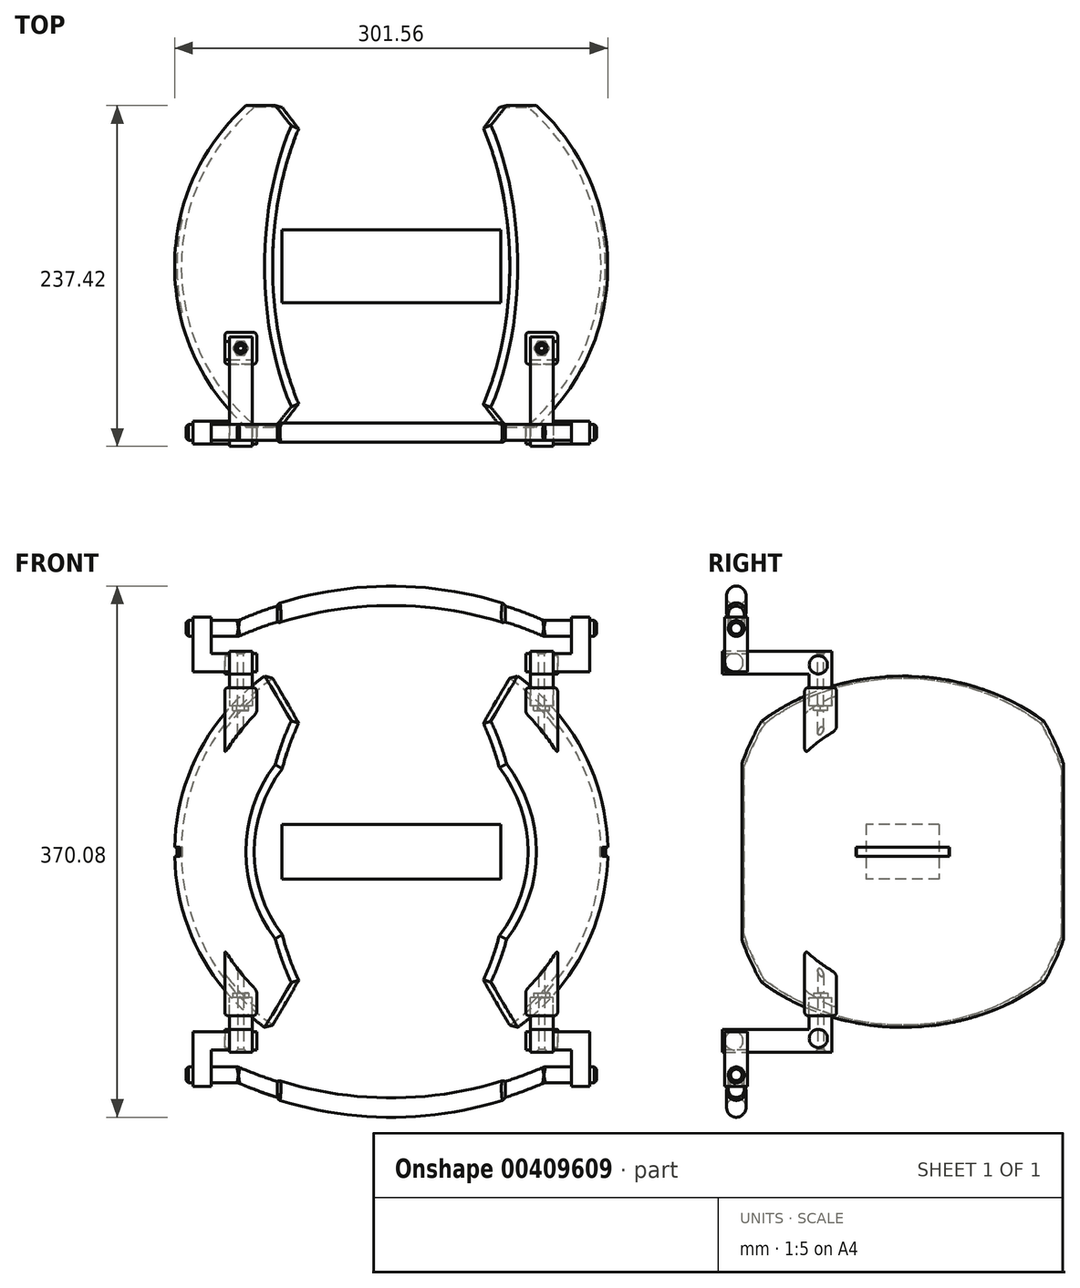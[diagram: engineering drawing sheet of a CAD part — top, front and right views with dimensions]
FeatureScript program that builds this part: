
annotation { "Feature Type Name" : "Feature", "Feature Type Description" : "" }
export const myFeature = defineFeature(function(context is Context, id is Id, definition is map)
    precondition{}
    {
        {
            var Q0;
            Q0=qCreatedBy(makeId("Right.planeOp"),FACE);
            var sketch = newSketch(context, id + "F0", { "sketchPlane" : qUnion([Q0])});
            skArc(sketch, "E0", {"start": v(0, -146.11) * mm, "mid": v(146.11, 0) * mm, "end": v(0, 146.11) * mm});
            skArc(sketch, "E1", {"start": v(0, -150.81) * mm, "mid": v(150.81, 0) * mm, "end": v(0, 150.81) * mm});
            skLineSegment(sketch, "E2", {"start": v(0, 150.81) * mm, "end": v(0, 146.11) * mm});
            skLineSegment(sketch, "E3.trimOffspring", {"start": v(0, 0) * mm, "end": v(0, -150.81) * mm});
            skSolve(sketch);
        }
        {
            var Q0;
            Q0 = qSketchRegion(id + "F0", true);
            var Q1;
            Q1=sQuery(id+"F0.wireOp",EDGE,"E3.trimOffspring");
            revolve(context, id + "F1", {"entities" : qUnion([Q0]), "axis" : qUnion([Q1]), "revolveType" : RevolveType.FULL});
        }
        {
            var Q0;
            Q0=qCreatedBy(makeId("Top.planeOp"),FACE);
            var sketch = newSketch(context, id + "F2", { "sketchPlane" : qUnion([Q0])});
            skEllipse(sketch, "E4", {"center": v(0, 0) * mm, "majorRadius": 152.4 * mm, "minorRadius": 82.55 * mm, "majorAxis": v(0, -1)});
            skSolve(sketch);
        }
        {
            var Q0;
            Q0 = qSketchRegion(id + "F2", true);
            extrude(context, id + "F3", {"entities" : qUnion([Q0]), "operationType" : NewBodyOperationType.REMOVE, "endBound" : BoundingType.SYMMETRIC, "oppositeDirection" : true, "depth" : 304.8 * mm});
        }
        {
            var Q0;
            Q0=qCreatedBy(makeId("Front.planeOp"),FACE);
            var sketch = newSketch(context, id + "F4", { "sketchPlane" : qUnion([Q0])});
            skArc(sketch, "E5", {"start": v(-74.85, 58.9) * mm, "mid": v(-95.25, 0) * mm, "end": v(-74.85, -58.9) * mm});
            skEllipticalArc(sketch, "E6", {});
            skEllipticalArc(sketch, "E7.trimOffspring", {});
            skArc(sketch, "E8.trimOffspring", {"start": v(74.85, -58.9) * mm, "mid": v(95.25, 0) * mm, "end": v(74.85, 58.9) * mm});
            const initialGuessF4  = {"E6": [0, 0, 0, -1, 0.1397, 0.08255, 5.147638887361655, 1.1355464198179313], "E7.trimOffspring": [0, 0, 0, -1, 0.1397, 0.08255, 2.006046233771862, 4.277139073407724]};
            skSetInitialGuess(sketch, initialGuessF4);
            skSolve(sketch);
        }
        {
            var Q0;
            Q0 = qSketchRegion(id + "F4", true);
            extrude(context, id + "F5", {"entities" : qUnion([Q0]), "operationType" : NewBodyOperationType.REMOVE, "endBound" : BoundingType.SYMMETRIC, "oppositeDirection" : true, "depth" : 304.8 * mm});
        }
        {
            var Q0;
            {var subQ0=makeQuery(id+"F1.opRevolve","SWEPT_FACE",FACE,{"disambiguationData":[OSD([sQuery(id+"F0.wireOp",EDGE,"E1")])]});var subQ1=makeQuery(id+"F3.opExtrude","SWEPT_FACE",FACE,{"disambiguationData":[OSD([sQuery(id+"F2.wireOp",EDGE,"E4")])]});Q0=makeQuery(id+"F5.boolean.opBoolean","SPLIT",EDGE,{"disambiguationData":[TD([makeQuery(id+"F5.opExtrude","SWEPT_FACE",FACE,{"disambiguationData":[OSD([sQuery(id+"F4.wireOp",EDGE,"E7.trimOffspring")])]})])],"derivedFrom":makeQuery(id+"F3.boolean.opBoolean","INTERSECT",EDGE,{"disambiguationData":[OD(1.0)],"derivedFrom":[subQ0,subQ1]})});}
            var Q1;
            Q1=makeQuery(id+"F5.boolean.opBoolean","INTERSECT",EDGE,{"disambiguationData":[OD(0.0)],"derivedFrom":[makeQuery(id+"F3.boolean.opBoolean","SPLIT",FACE,{"disambiguationData":[OD(1.0)],"derivedFrom":makeQuery(id+"F1.opRevolve","SWEPT_FACE",FACE,{"disambiguationData":[OSD([sQuery(id+"F0.wireOp",EDGE,"E1")])]})}),makeQuery(id+"F5.opExtrude","SWEPT_FACE",FACE,{"disambiguationData":[OSD([sQuery(id+"F4.wireOp",EDGE,"E5")])]})]});
            var Q2;
            Q2=makeQuery(id+"F5.boolean.opBoolean","INTERSECT",EDGE,{"disambiguationData":[OD(1.0)],"derivedFrom":[makeQuery(id+"F3.boolean.opBoolean","SPLIT",FACE,{"disambiguationData":[OD(1.0)],"derivedFrom":makeQuery(id+"F1.opRevolve","SWEPT_FACE",FACE,{"disambiguationData":[OSD([sQuery(id+"F0.wireOp",EDGE,"E1")])]})}),makeQuery(id+"F5.opExtrude","SWEPT_FACE",FACE,{"disambiguationData":[OSD([sQuery(id+"F4.wireOp",EDGE,"E5")])]})]});
            var Q3;
            {var subQ0=makeQuery(id+"F1.opRevolve","SWEPT_FACE",FACE,{"disambiguationData":[OSD([sQuery(id+"F0.wireOp",EDGE,"E1")])]});var subQ1=makeQuery(id+"F3.opExtrude","SWEPT_FACE",FACE,{"disambiguationData":[OSD([sQuery(id+"F2.wireOp",EDGE,"E4")])]});Q3=makeQuery(id+"F5.boolean.opBoolean","SPLIT",EDGE,{"disambiguationData":[TD([makeQuery(id+"F5.opExtrude","SWEPT_FACE",FACE,{"disambiguationData":[OSD([sQuery(id+"F4.wireOp",EDGE,"E6")])]})])],"derivedFrom":makeQuery(id+"F3.boolean.opBoolean","INTERSECT",EDGE,{"disambiguationData":[OD(1.0)],"derivedFrom":[subQ0,subQ1]})});}
            var Q4;
            {var subQ0=makeQuery(id+"F1.opRevolve","SWEPT_FACE",FACE,{"disambiguationData":[OSD([sQuery(id+"F0.wireOp",EDGE,"E1")])]});var subQ1=makeQuery(id+"F3.opExtrude","SWEPT_FACE",FACE,{"disambiguationData":[OSD([sQuery(id+"F2.wireOp",EDGE,"E4")])]});Q4=makeQuery(id+"F5.boolean.opBoolean","SPLIT",EDGE,{"disambiguationData":[TD([makeQuery(id+"F5.opExtrude","SWEPT_FACE",FACE,{"disambiguationData":[OSD([sQuery(id+"F4.wireOp",EDGE,"E7.trimOffspring")])]})])],"derivedFrom":makeQuery(id+"F3.boolean.opBoolean","INTERSECT",EDGE,{"disambiguationData":[OD(0.0)],"derivedFrom":[subQ0,subQ1]})});}
            var Q5;
            Q5=makeQuery(id+"F5.boolean.opBoolean","INTERSECT",EDGE,{"disambiguationData":[OD(1.0)],"derivedFrom":[makeQuery(id+"F3.boolean.opBoolean","SPLIT",FACE,{"disambiguationData":[OD(0.0)],"derivedFrom":makeQuery(id+"F1.opRevolve","SWEPT_FACE",FACE,{"disambiguationData":[OSD([sQuery(id+"F0.wireOp",EDGE,"E1")])]})}),makeQuery(id+"F5.opExtrude","SWEPT_FACE",FACE,{"disambiguationData":[OSD([sQuery(id+"F4.wireOp",EDGE,"E8.trimOffspring")])]})]});
            var Q6;
            Q6=makeQuery(id+"F5.boolean.opBoolean","INTERSECT",EDGE,{"disambiguationData":[OD(0.0)],"derivedFrom":[makeQuery(id+"F3.boolean.opBoolean","SPLIT",FACE,{"disambiguationData":[OD(0.0)],"derivedFrom":makeQuery(id+"F1.opRevolve","SWEPT_FACE",FACE,{"disambiguationData":[OSD([sQuery(id+"F0.wireOp",EDGE,"E1")])]})}),makeQuery(id+"F5.opExtrude","SWEPT_FACE",FACE,{"disambiguationData":[OSD([sQuery(id+"F4.wireOp",EDGE,"E8.trimOffspring")])]})]});
            var Q7;
            {var subQ0=makeQuery(id+"F1.opRevolve","SWEPT_FACE",FACE,{"disambiguationData":[OSD([sQuery(id+"F0.wireOp",EDGE,"E1")])]});var subQ1=makeQuery(id+"F3.opExtrude","SWEPT_FACE",FACE,{"disambiguationData":[OSD([sQuery(id+"F2.wireOp",EDGE,"E4")])]});Q7=makeQuery(id+"F5.boolean.opBoolean","SPLIT",EDGE,{"disambiguationData":[TD([makeQuery(id+"F5.opExtrude","SWEPT_FACE",FACE,{"disambiguationData":[OSD([sQuery(id+"F4.wireOp",EDGE,"E6")])]})])],"derivedFrom":makeQuery(id+"F3.boolean.opBoolean","INTERSECT",EDGE,{"disambiguationData":[OD(0.0)],"derivedFrom":[subQ0,subQ1]})});}
            chamfer(context, id + "F6", {"entities" : qUnion([Q0, Q1, Q2, Q3, Q4, Q5, Q6, Q7]), "chamferType" : ChamferType.OFFSET_ANGLE, "width" : 7.62 * mm, "oppositeDirection" : false, "angle" : 55 * degree, "tangentPropagation" : true});
        }
        {
            var Q0;
            Q0=makeQuery(id+"F5.boolean.opBoolean","INTERSECT",EDGE,{"disambiguationData":[OD(0.0)],"derivedFrom":[makeQuery(id+"F3.boolean.opBoolean","SPLIT",FACE,{"disambiguationData":[OD(1.0)],"derivedFrom":makeQuery(id+"F1.opRevolve","SWEPT_FACE",FACE,{"disambiguationData":[OSD([sQuery(id+"F0.wireOp",EDGE,"E1")])]})}),makeQuery(id+"F5.opExtrude","SWEPT_FACE",FACE,{"disambiguationData":[OSD([sQuery(id+"F4.wireOp",EDGE,"E7.trimOffspring")])]})]});
            var Q1;
            Q1=makeQuery(id+"F5.boolean.opBoolean","INTERSECT",EDGE,{"disambiguationData":[OD(1.0)],"derivedFrom":[makeQuery(id+"F3.boolean.opBoolean","SPLIT",FACE,{"disambiguationData":[OD(1.0)],"derivedFrom":makeQuery(id+"F1.opRevolve","SWEPT_FACE",FACE,{"disambiguationData":[OSD([sQuery(id+"F0.wireOp",EDGE,"E1")])]})}),makeQuery(id+"F5.opExtrude","SWEPT_FACE",FACE,{"disambiguationData":[OSD([sQuery(id+"F4.wireOp",EDGE,"E7.trimOffspring")])]})]});
            var Q2;
            Q2=makeQuery(id+"F5.boolean.opBoolean","INTERSECT",EDGE,{"disambiguationData":[OD(1.0)],"derivedFrom":[makeQuery(id+"F3.boolean.opBoolean","SPLIT",FACE,{"disambiguationData":[OD(1.0)],"derivedFrom":makeQuery(id+"F1.opRevolve","SWEPT_FACE",FACE,{"disambiguationData":[OSD([sQuery(id+"F0.wireOp",EDGE,"E1")])]})}),makeQuery(id+"F5.opExtrude","SWEPT_FACE",FACE,{"disambiguationData":[OSD([sQuery(id+"F4.wireOp",EDGE,"E6")])]})]});
            var Q3;
            Q3=makeQuery(id+"F5.boolean.opBoolean","INTERSECT",EDGE,{"disambiguationData":[OD(0.0)],"derivedFrom":[makeQuery(id+"F3.boolean.opBoolean","SPLIT",FACE,{"disambiguationData":[OD(1.0)],"derivedFrom":makeQuery(id+"F1.opRevolve","SWEPT_FACE",FACE,{"disambiguationData":[OSD([sQuery(id+"F0.wireOp",EDGE,"E1")])]})}),makeQuery(id+"F5.opExtrude","SWEPT_FACE",FACE,{"disambiguationData":[OSD([sQuery(id+"F4.wireOp",EDGE,"E6")])]})]});
            var Q4;
            Q4=makeQuery(id+"F5.boolean.opBoolean","INTERSECT",EDGE,{"disambiguationData":[OD(0.0)],"derivedFrom":[makeQuery(id+"F3.boolean.opBoolean","SPLIT",FACE,{"disambiguationData":[OD(0.0)],"derivedFrom":makeQuery(id+"F1.opRevolve","SWEPT_FACE",FACE,{"disambiguationData":[OSD([sQuery(id+"F0.wireOp",EDGE,"E1")])]})}),makeQuery(id+"F5.opExtrude","SWEPT_FACE",FACE,{"disambiguationData":[OSD([sQuery(id+"F4.wireOp",EDGE,"E7.trimOffspring")])]})]});
            var Q5;
            Q5=makeQuery(id+"F5.boolean.opBoolean","INTERSECT",EDGE,{"disambiguationData":[OD(1.0)],"derivedFrom":[makeQuery(id+"F3.boolean.opBoolean","SPLIT",FACE,{"disambiguationData":[OD(0.0)],"derivedFrom":makeQuery(id+"F1.opRevolve","SWEPT_FACE",FACE,{"disambiguationData":[OSD([sQuery(id+"F0.wireOp",EDGE,"E1")])]})}),makeQuery(id+"F5.opExtrude","SWEPT_FACE",FACE,{"disambiguationData":[OSD([sQuery(id+"F4.wireOp",EDGE,"E7.trimOffspring")])]})]});
            var Q6;
            Q6=makeQuery(id+"F5.boolean.opBoolean","INTERSECT",EDGE,{"disambiguationData":[OD(0.0)],"derivedFrom":[makeQuery(id+"F3.boolean.opBoolean","SPLIT",FACE,{"disambiguationData":[OD(0.0)],"derivedFrom":makeQuery(id+"F1.opRevolve","SWEPT_FACE",FACE,{"disambiguationData":[OSD([sQuery(id+"F0.wireOp",EDGE,"E1")])]})}),makeQuery(id+"F5.opExtrude","SWEPT_FACE",FACE,{"disambiguationData":[OSD([sQuery(id+"F4.wireOp",EDGE,"E6")])]})]});
            var Q7;
            Q7=makeQuery(id+"F5.boolean.opBoolean","INTERSECT",EDGE,{"disambiguationData":[OD(1.0)],"derivedFrom":[makeQuery(id+"F3.boolean.opBoolean","SPLIT",FACE,{"disambiguationData":[OD(0.0)],"derivedFrom":makeQuery(id+"F1.opRevolve","SWEPT_FACE",FACE,{"disambiguationData":[OSD([sQuery(id+"F0.wireOp",EDGE,"E1")])]})}),makeQuery(id+"F5.opExtrude","SWEPT_FACE",FACE,{"disambiguationData":[OSD([sQuery(id+"F4.wireOp",EDGE,"E6")])]})]});
            chamfer(context, id + "F7", {"entities" : qUnion([Q0, Q1, Q2, Q3, Q4, Q5, Q6, Q7]), "chamferType" : ChamferType.OFFSET_ANGLE, "width" : 7.62 * mm, "oppositeDirection" : false, "angle" : 55 * degree, "tangentPropagation" : true});
        }
        {
            var Q0;
            Q0=qCreatedBy(makeId("Front.planeOp"),FACE);
            var sketch = newSketch(context, id + "F8", { "sketchPlane" : qUnion([Q0])});
            skLineSegment(sketch, "E9", {"start": v(-149.23, 0) * mm, "end": v(149.23, 0) * mm});
            skLineSegment(sketch, "E10", {"start": v(-149.2, 3.1) * mm, "end": v(-152.4, 3.18) * mm});
            skLineSegment(sketch, "E11", {"start": v(-149.2, -3.1) * mm, "end": v(-152.4, -3.18) * mm});
            skLineSegment(sketch, "E12", {"start": v(149.2, 3.1) * mm, "end": v(152.4, 3.17) * mm});
            skLineSegment(sketch, "E13", {"start": v(149.2, -3.1) * mm, "end": v(152.4, -3.18) * mm});
            skLineSegment(sketch, "E14", {"start": v(-152.4, 3.18) * mm, "end": v(-152.4, -3.18) * mm});
            skLineSegment(sketch, "E15", {"start": v(152.4, 0) * mm, "end": v(152.4, 3.18) * mm});
            skLineSegment(sketch, "E16", {"start": v(152.4, 0) * mm, "end": v(152.4, -3.17) * mm});
            skPoint(sketch, "E17.orphan", {"position": v(-174.04, 0) * mm});
            skArc(sketch, "E18", {"start": v(-149.2, 3.1) * mm, "mid": v(-149.23, 0) * mm, "end": v(-149.2, -3.1) * mm});
            skArc(sketch, "E19.trimOffspring", {"start": v(149.2, -3.1) * mm, "mid": v(149.23, 0) * mm, "end": v(149.2, 3.1) * mm});
            skLineSegment(sketch, "E20", {"start": v(0, -61.34) * mm, "end": v(0, 25.34) * mm});
            skSolve(sketch);
        }
        {
            var Q0;
            Q0 = qSketchRegion(id + "F8", true);
            var Q1;
            Q1=sQuery(id+"F8.wireOp",EDGE,"E20");
            revolve(context, id + "F9", {"operationType" : NewBodyOperationType.REMOVE, "entities" : qUnion([Q0]), "axis" : qUnion([Q1]), "revolveType" : RevolveType.SYMMETRIC, "angle" : 25 * degree});
        }
        {
            var Q0;
            Q0=qCreatedBy(makeId("Top.planeOp"),FACE);
            cPlane(context, id + "F10", {"entities" : qUnion([Q0]), "cplaneType" : CPlaneType.OFFSET, "offset" : 127 * mm, "width" : 152.4 * mm, "height" : 152.4 * mm});
        }
        {
            var Q0;
            Q0=qCreatedBy(makeId("Top.planeOp"),FACE);
            cPlane(context, id + "F11", {"entities" : qUnion([Q0]), "cplaneType" : CPlaneType.OFFSET, "offset" : 127 * mm, "oppositeDirection" : true, "width" : 152.4 * mm, "height" : 152.4 * mm});
        }
        {
            var Q0;
            Q0=qCreatedBy(id+"F10.planeOp",FACE);
            var sketch = newSketch(context, id + "F12", { "sketchPlane" : qUnion([Q0])});
            skPoint(sketch, "E21", {"position": v(-104.78, -57.15) * mm});
            skPoint(sketch, "E22", {"position": v(104.77, -57.15) * mm});
            skLineSegment(sketch, "E23.bottom", {"start": v(-93.66, -46.04) * mm, "end": v(-115.89, -46.04) * mm});
            skLineSegment(sketch, "E23.top", {"start": v(-93.66, -68.26) * mm, "end": v(-115.89, -68.26) * mm});
            skLineSegment(sketch, "E23.left", {"start": v(-93.66, -46.04) * mm, "end": v(-93.66, -68.26) * mm});
            skLineSegment(sketch, "E23.right", {"start": v(-115.89, -46.04) * mm, "end": v(-115.89, -68.26) * mm});
            skLineSegment(sketch, "E24.bottom", {"start": v(93.66, -46.04) * mm, "end": v(115.89, -46.04) * mm});
            skLineSegment(sketch, "E24.top", {"start": v(93.66, -68.26) * mm, "end": v(115.89, -68.26) * mm});
            skLineSegment(sketch, "E24.left", {"start": v(93.66, -46.04) * mm, "end": v(93.66, -68.26) * mm});
            skLineSegment(sketch, "E24.right", {"start": v(115.89, -46.04) * mm, "end": v(115.89, -68.26) * mm});
            skSolve(sketch);
        }
        {
            var Q0;
            Q0 = qSketchRegion(id + "F12", true);
            var Q1;
            Q1=makeQuery(id+"F3.boolean.opBoolean","SPLIT",FACE,{"disambiguationData":[OD(1.0)],"derivedFrom":makeQuery(id+"F1.opRevolve","SWEPT_FACE",FACE,{"disambiguationData":[OSD([sQuery(id+"F0.wireOp",EDGE,"E1")])]})});
            var Q2;
            Q2=makeQuery(id+"F3.boolean.opBoolean","SPLIT",FACE,{"disambiguationData":[OD(1.0)],"derivedFrom":makeQuery(id+"F1.opRevolve","SWEPT_FACE",FACE,{"disambiguationData":[OSD([sQuery(id+"F0.wireOp",EDGE,"E1")])]})});
            extrude(context, id + "F13", {"entities" : qUnion([Q0]), "operationType" : NewBodyOperationType.ADD, "endBound" : BoundingType.UP_TO_SURFACE, "oppositeDirection" : true, "endBoundEntityFace" : qUnion([Q1]), "depth" : 17.78 * mm, "hasSecondDirection" : true, "secondDirectionOppositeDirection" : true, "secondDirectionBoundEntityFace" : qUnion([Q2]), "secondDirectionDepth" : 12.7 * mm});
        }
        {
            var Q0;
            Q0=qCreatedBy(id+"F11.planeOp",FACE);
            var sketch = newSketch(context, id + "F14", { "sketchPlane" : qUnion([Q0])});
            skPoint(sketch, "E25", {"position": v(-104.77, -57.15) * mm});
            skPoint(sketch, "E26", {"position": v(104.78, -57.15) * mm});
            skLineSegment(sketch, "E27.bottom", {"start": v(-93.66, -46.04) * mm, "end": v(-115.89, -46.04) * mm});
            skLineSegment(sketch, "E27.top", {"start": v(-93.66, -68.26) * mm, "end": v(-115.89, -68.26) * mm});
            skLineSegment(sketch, "E27.left", {"start": v(-93.66, -46.04) * mm, "end": v(-93.66, -68.26) * mm});
            skLineSegment(sketch, "E27.right", {"start": v(-115.89, -46.04) * mm, "end": v(-115.89, -68.26) * mm});
            skLineSegment(sketch, "E28.bottom", {"start": v(93.66, -46.04) * mm, "end": v(115.89, -46.04) * mm});
            skLineSegment(sketch, "E28.top", {"start": v(93.66, -68.26) * mm, "end": v(115.89, -68.26) * mm});
            skLineSegment(sketch, "E28.left", {"start": v(93.66, -46.04) * mm, "end": v(93.66, -68.26) * mm});
            skLineSegment(sketch, "E28.right", {"start": v(115.89, -46.04) * mm, "end": v(115.89, -68.26) * mm});
            skSolve(sketch);
        }
        {
            var Q0;
            Q0 = qSketchRegion(id + "F14", true);
            var Q1;
            Q1=makeQuery(id+"F3.boolean.opBoolean","SPLIT",FACE,{"disambiguationData":[OD(1.0)],"derivedFrom":makeQuery(id+"F1.opRevolve","SWEPT_FACE",FACE,{"disambiguationData":[OSD([sQuery(id+"F0.wireOp",EDGE,"E1")])]})});
            extrude(context, id + "F15", {"entities" : qUnion([Q0]), "operationType" : NewBodyOperationType.ADD, "endBound" : BoundingType.UP_TO_SURFACE, "endBoundEntityFace" : qUnion([Q1]), "depth" : 25.4 * mm, "hasSecondDirection" : true, "secondDirectionOppositeDirection" : false, "secondDirectionDepth" : 12.7 * mm});
        }
        {
            var Q0;
            Q0=makeQuery(id+"F13.opExtrude","SWEPT_EDGE",EDGE,{"disambiguationData":[OSD([sQuery(id+"F12.wireOp",EDGE,"E23.top"),sQuery(id+"F12.wireOp",EDGE,"E23.right")])]});
            var Q1;
            Q1=makeQuery(id+"F13.opExtrude","SWEPT_EDGE",EDGE,{"disambiguationData":[OSD([sQuery(id+"F12.wireOp",EDGE,"E23.top"),sQuery(id+"F12.wireOp",EDGE,"E23.left")])]});
            var Q2;
            Q2=makeQuery(id+"F13.opExtrude","SWEPT_EDGE",EDGE,{"disambiguationData":[OSD([sQuery(id+"F12.wireOp",EDGE,"E23.bottom"),sQuery(id+"F12.wireOp",EDGE,"E23.left")])]});
            var Q3;
            Q3=makeQuery(id+"F13.opExtrude","SWEPT_EDGE",EDGE,{"disambiguationData":[OSD([sQuery(id+"F12.wireOp",EDGE,"E23.bottom"),sQuery(id+"F12.wireOp",EDGE,"E23.right")])]});
            var Q4;
            Q4=makeQuery(id+"F13.opExtrude","CAP_EDGE",EDGE,{"disambiguationData":[OSD([sQuery(id+"F12.wireOp",EDGE,"E23.right")])],"isStart":true});
            var Q5;
            Q5=makeQuery(id+"F13.opExtrude","CAP_EDGE",EDGE,{"disambiguationData":[OSD([sQuery(id+"F12.wireOp",EDGE,"E23.bottom")])],"isStart":true});
            var Q6;
            Q6=makeQuery(id+"F13.opExtrude","CAP_EDGE",EDGE,{"disambiguationData":[OSD([sQuery(id+"F12.wireOp",EDGE,"E23.left")])],"isStart":true});
            var Q7;
            Q7=makeQuery(id+"F13.opExtrude","CAP_EDGE",EDGE,{"disambiguationData":[OSD([sQuery(id+"F12.wireOp",EDGE,"E23.top")])],"isStart":true});
            var Q8;
            Q8=makeQuery(id+"F13.opExtrude","SWEPT_EDGE",EDGE,{"disambiguationData":[OSD([sQuery(id+"F12.wireOp",EDGE,"E24.bottom"),sQuery(id+"F12.wireOp",EDGE,"E24.left")])]});
            var Q9;
            Q9=makeQuery(id+"F13.opExtrude","SWEPT_EDGE",EDGE,{"disambiguationData":[OSD([sQuery(id+"F12.wireOp",EDGE,"E24.top"),sQuery(id+"F12.wireOp",EDGE,"E24.left")])]});
            var Q10;
            Q10=makeQuery(id+"F13.opExtrude","SWEPT_EDGE",EDGE,{"disambiguationData":[OSD([sQuery(id+"F12.wireOp",EDGE,"E24.top"),sQuery(id+"F12.wireOp",EDGE,"E24.right")])]});
            var Q11;
            Q11=makeQuery(id+"F13.opExtrude","SWEPT_EDGE",EDGE,{"disambiguationData":[OSD([sQuery(id+"F12.wireOp",EDGE,"E24.bottom"),sQuery(id+"F12.wireOp",EDGE,"E24.right")])]});
            var Q12;
            Q12=makeQuery(id+"F13.opExtrude","CAP_EDGE",EDGE,{"disambiguationData":[OSD([sQuery(id+"F12.wireOp",EDGE,"E24.bottom")])],"isStart":true});
            var Q13;
            Q13=makeQuery(id+"F13.opExtrude","CAP_EDGE",EDGE,{"disambiguationData":[OSD([sQuery(id+"F12.wireOp",EDGE,"E24.left")])],"isStart":true});
            var Q14;
            Q14=makeQuery(id+"F13.opExtrude","CAP_EDGE",EDGE,{"disambiguationData":[OSD([sQuery(id+"F12.wireOp",EDGE,"E24.top")])],"isStart":true});
            var Q15;
            Q15=makeQuery(id+"F13.opExtrude","CAP_EDGE",EDGE,{"disambiguationData":[OSD([sQuery(id+"F12.wireOp",EDGE,"E24.right")])],"isStart":true});
            var Q16;
            Q16=makeQuery(id+"F15.opExtrude","SWEPT_EDGE",EDGE,{"disambiguationData":[OSD([sQuery(id+"F14.wireOp",EDGE,"E27.bottom"),sQuery(id+"F14.wireOp",EDGE,"E27.right")])]});
            var Q17;
            Q17=makeQuery(id+"F15.opExtrude","SWEPT_EDGE",EDGE,{"disambiguationData":[OSD([sQuery(id+"F14.wireOp",EDGE,"E27.top"),sQuery(id+"F14.wireOp",EDGE,"E27.right")])]});
            var Q18;
            Q18=makeQuery(id+"F15.opExtrude","SWEPT_EDGE",EDGE,{"disambiguationData":[OSD([sQuery(id+"F14.wireOp",EDGE,"E27.top"),sQuery(id+"F14.wireOp",EDGE,"E27.left")])]});
            var Q19;
            Q19=makeQuery(id+"F15.opExtrude","SWEPT_EDGE",EDGE,{"disambiguationData":[OSD([sQuery(id+"F14.wireOp",EDGE,"E27.bottom"),sQuery(id+"F14.wireOp",EDGE,"E27.left")])]});
            var Q20;
            Q20=makeQuery(id+"F15.opExtrude","CAP_EDGE",EDGE,{"disambiguationData":[OSD([sQuery(id+"F14.wireOp",EDGE,"E27.right")])],"isStart":true});
            var Q21;
            Q21=makeQuery(id+"F15.opExtrude","CAP_EDGE",EDGE,{"disambiguationData":[OSD([sQuery(id+"F14.wireOp",EDGE,"E27.bottom")])],"isStart":true});
            var Q22;
            Q22=makeQuery(id+"F15.opExtrude","CAP_EDGE",EDGE,{"disambiguationData":[OSD([sQuery(id+"F14.wireOp",EDGE,"E27.top")])],"isStart":true});
            var Q23;
            Q23=makeQuery(id+"F15.opExtrude","CAP_EDGE",EDGE,{"disambiguationData":[OSD([sQuery(id+"F14.wireOp",EDGE,"E27.left")])],"isStart":true});
            var Q24;
            Q24=makeQuery(id+"F15.opExtrude","SWEPT_EDGE",EDGE,{"disambiguationData":[OSD([sQuery(id+"F14.wireOp",EDGE,"E28.top"),sQuery(id+"F14.wireOp",EDGE,"E28.left")])]});
            var Q25;
            Q25=makeQuery(id+"F15.opExtrude","SWEPT_EDGE",EDGE,{"disambiguationData":[OSD([sQuery(id+"F14.wireOp",EDGE,"E28.top"),sQuery(id+"F14.wireOp",EDGE,"E28.right")])]});
            var Q26;
            Q26=makeQuery(id+"F15.opExtrude","SWEPT_EDGE",EDGE,{"disambiguationData":[OSD([sQuery(id+"F14.wireOp",EDGE,"E28.bottom"),sQuery(id+"F14.wireOp",EDGE,"E28.right")])]});
            var Q27;
            Q27=makeQuery(id+"F15.opExtrude","SWEPT_EDGE",EDGE,{"disambiguationData":[OSD([sQuery(id+"F14.wireOp",EDGE,"E28.bottom"),sQuery(id+"F14.wireOp",EDGE,"E28.left")])]});
            var Q28;
            Q28=makeQuery(id+"F15.opExtrude","CAP_EDGE",EDGE,{"disambiguationData":[OSD([sQuery(id+"F14.wireOp",EDGE,"E28.left")])],"isStart":true});
            var Q29;
            Q29=makeQuery(id+"F15.opExtrude","CAP_EDGE",EDGE,{"disambiguationData":[OSD([sQuery(id+"F14.wireOp",EDGE,"E28.top")])],"isStart":true});
            var Q30;
            Q30=makeQuery(id+"F15.opExtrude","CAP_EDGE",EDGE,{"disambiguationData":[OSD([sQuery(id+"F14.wireOp",EDGE,"E28.right")])],"isStart":true});
            var Q31;
            Q31=makeQuery(id+"F15.opExtrude","CAP_EDGE",EDGE,{"disambiguationData":[OSD([sQuery(id+"F14.wireOp",EDGE,"E28.bottom")])],"isStart":true});
            fillet(context, id + "F16", {"entities" : qUnion([Q0, Q1, Q2, Q3, Q4, Q5, Q6, Q7, Q8, Q9, Q10, Q11, Q12, Q13, Q14, Q15, Q16, Q17, Q18, Q19, Q20, Q21, Q22, Q23, Q24, Q25, Q26, Q27, Q28, Q29, Q30, Q31]), "radius" : 2.38 * mm, "tangentPropagation" : true, "allowEdgeOverflow" : false});
        }
        {
            var Q0;
            Q0=makeQuery(id+"F13.opExtrude","CAP_FACE",FACE,{"disambiguationData":[OSD([sQuery(id+"F12.wireOp",EDGE,"E24.bottom"),sQuery(id+"F12.wireOp",EDGE,"E24.top"),sQuery(id+"F12.wireOp",EDGE,"E24.left"),sQuery(id+"F12.wireOp",EDGE,"E24.right")])],"isStart":true});
            var sketch = newSketch(context, id + "F17", { "sketchPlane" : qUnion([Q0])});
            skLineSegment(sketch, "E29", {"start": v(96.05, -57.15) * mm, "end": v(113.5, -57.15) * mm});
            skLineSegment(sketch, "E30.bottom", {"start": v(112.71, -49.21) * mm, "end": v(96.84, -49.21) * mm});
            skLineSegment(sketch, "E30.top", {"start": v(112.71, -65.09) * mm, "end": v(96.84, -65.09) * mm});
            skLineSegment(sketch, "E30.left", {"start": v(112.71, -49.21) * mm, "end": v(112.71, -65.09) * mm});
            skLineSegment(sketch, "E30.right", {"start": v(96.84, -49.21) * mm, "end": v(96.84, -65.09) * mm});
            skPoint(sketch, "E30.middle", {"position": v(104.77, -57.15) * mm});
            skSolve(sketch);
        }
        {
            var Q0;
            Q0=makeQuery(id+"F13.opExtrude","CAP_FACE",FACE,{"disambiguationData":[OSD([sQuery(id+"F12.wireOp",EDGE,"E23.bottom"),sQuery(id+"F12.wireOp",EDGE,"E23.top"),sQuery(id+"F12.wireOp",EDGE,"E23.left"),sQuery(id+"F12.wireOp",EDGE,"E23.right")])],"isStart":true});
            var sketch = newSketch(context, id + "F18", { "sketchPlane" : qUnion([Q0])});
            skLineSegment(sketch, "E31", {"start": v(-113.5, -57.15) * mm, "end": v(-96.05, -57.15) * mm});
            skLineSegment(sketch, "E32.bottom", {"start": v(-96.84, -49.21) * mm, "end": v(-112.71, -49.21) * mm});
            skLineSegment(sketch, "E32.top", {"start": v(-96.84, -65.09) * mm, "end": v(-112.71, -65.09) * mm});
            skLineSegment(sketch, "E32.left", {"start": v(-96.84, -49.21) * mm, "end": v(-96.84, -65.09) * mm});
            skLineSegment(sketch, "E32.right", {"start": v(-112.71, -49.21) * mm, "end": v(-112.71, -65.09) * mm});
            skPoint(sketch, "E32.middle", {"position": v(-104.78, -57.15) * mm});
            skSolve(sketch);
        }
        {
            var Q0;
            Q0 = qSketchRegion(id + "F18", true);
            var Q1;
            Q1 = qSketchRegion(id + "F17", true);
            extrude(context, id + "F19", {"entities" : qUnion([Q0, Q1]), "operationType" : NewBodyOperationType.REMOVE, "oppositeDirection" : true, "depth" : 12.7 * mm});
        }
        {
            var Q0;
            Q0=makeQuery(id+"F15.opExtrude","CAP_FACE",FACE,{"disambiguationData":[OSD([sQuery(id+"F14.wireOp",EDGE,"E28.bottom"),sQuery(id+"F14.wireOp",EDGE,"E28.top"),sQuery(id+"F14.wireOp",EDGE,"E28.left"),sQuery(id+"F14.wireOp",EDGE,"E28.right")])],"isStart":true});
            var sketch = newSketch(context, id + "F20", { "sketchPlane" : qUnion([Q0])});
            skLineSegment(sketch, "E33", {"start": v(96.05, 57.15) * mm, "end": v(113.5, 57.15) * mm});
            skLineSegment(sketch, "E34.bottom", {"start": v(112.71, 65.09) * mm, "end": v(96.84, 65.09) * mm});
            skLineSegment(sketch, "E34.top", {"start": v(112.71, 49.21) * mm, "end": v(96.84, 49.21) * mm});
            skLineSegment(sketch, "E34.left", {"start": v(112.71, 65.09) * mm, "end": v(112.71, 49.21) * mm});
            skLineSegment(sketch, "E34.right", {"start": v(96.84, 65.09) * mm, "end": v(96.84, 49.21) * mm});
            skPoint(sketch, "E34.middle", {"position": v(104.78, 57.15) * mm});
            skSolve(sketch);
        }
        {
            var Q0;
            Q0=makeQuery(id+"F15.opExtrude","CAP_FACE",FACE,{"disambiguationData":[OSD([sQuery(id+"F14.wireOp",EDGE,"E27.bottom"),sQuery(id+"F14.wireOp",EDGE,"E27.top"),sQuery(id+"F14.wireOp",EDGE,"E27.left"),sQuery(id+"F14.wireOp",EDGE,"E27.right")])],"isStart":true});
            var sketch = newSketch(context, id + "F21", { "sketchPlane" : qUnion([Q0])});
            skLineSegment(sketch, "E35", {"start": v(-113.5, 57.15) * mm, "end": v(-96.05, 57.15) * mm});
            skLineSegment(sketch, "E36.bottom", {"start": v(-96.84, 65.09) * mm, "end": v(-112.71, 65.09) * mm});
            skLineSegment(sketch, "E36.top", {"start": v(-96.84, 49.21) * mm, "end": v(-112.71, 49.21) * mm});
            skLineSegment(sketch, "E36.left", {"start": v(-96.84, 65.09) * mm, "end": v(-96.84, 49.21) * mm});
            skLineSegment(sketch, "E36.right", {"start": v(-112.71, 65.09) * mm, "end": v(-112.71, 49.21) * mm});
            skPoint(sketch, "E36.middle", {"position": v(-104.78, 57.15) * mm});
            skSolve(sketch);
        }
        {
            var Q0;
            Q0 = qSketchRegion(id + "F20", true);
            var Q1;
            Q1 = qSketchRegion(id + "F21", true);
            extrude(context, id + "F22", {"entities" : qUnion([Q0, Q1]), "operationType" : NewBodyOperationType.REMOVE, "oppositeDirection" : true, "depth" : 12.7 * mm});
        }
        {
            var Q0;
            Q0=makeQuery(id+"F19.boolean.opBoolean","COPY",FACE,{"derivedFrom":makeQuery(id+"F19.opExtrude","CAP_FACE",FACE,{"disambiguationData":[OSD([sQuery(id+"F17.wireOp",EDGE,"E30.bottom"),sQuery(id+"F17.wireOp",EDGE,"E30.top"),sQuery(id+"F17.wireOp",EDGE,"E30.left"),sQuery(id+"F17.wireOp",EDGE,"E30.right")])],"isStart":false})});
            var sketch = newSketch(context, id + "F23", { "sketchPlane" : qUnion([Q0])});
            skLineSegment(sketch, "E37", {"start": v(96.84, -57.15) * mm, "end": v(112.71, -57.15) * mm});
            skCircle(sketch, "E38", {"center": v(104.77, -57.15) * mm, "radius": 2 * mm});
            skSolve(sketch);
        }
        {
            var Q0;
            Q0=makeQuery(id+"F19.boolean.opBoolean","COPY",FACE,{"derivedFrom":makeQuery(id+"F19.opExtrude","CAP_FACE",FACE,{"disambiguationData":[OSD([sQuery(id+"F18.wireOp",EDGE,"E32.bottom"),sQuery(id+"F18.wireOp",EDGE,"E32.top"),sQuery(id+"F18.wireOp",EDGE,"E32.left"),sQuery(id+"F18.wireOp",EDGE,"E32.right")])],"isStart":false})});
            var sketch = newSketch(context, id + "F24", { "sketchPlane" : qUnion([Q0])});
            skLineSegment(sketch, "E39", {"start": v(-112.71, -57.15) * mm, "end": v(-96.84, -57.15) * mm});
            skCircle(sketch, "E40", {"center": v(-104.78, -57.15) * mm, "radius": 2 * mm});
            skSolve(sketch);
        }
        {
            var Q0;
            Q0 = qSketchRegion(id + "F23", true);
            var Q1;
            Q1 = qSketchRegion(id + "F24", true);
            extrude(context, id + "F25", {"entities" : qUnion([Q0, Q1]), "operationType" : NewBodyOperationType.REMOVE, "oppositeDirection" : true, "depth" : 25.4 * mm});
        }
        {
            var Q0;
            Q0=makeQuery(id+"F22.boolean.opBoolean","COPY",FACE,{"derivedFrom":makeQuery(id+"F22.opExtrude","CAP_FACE",FACE,{"disambiguationData":[OSD([sQuery(id+"F20.wireOp",EDGE,"E34.bottom"),sQuery(id+"F20.wireOp",EDGE,"E34.top"),sQuery(id+"F20.wireOp",EDGE,"E34.left"),sQuery(id+"F20.wireOp",EDGE,"E34.right")])],"isStart":false})});
            var sketch = newSketch(context, id + "F26", { "sketchPlane" : qUnion([Q0])});
            skLineSegment(sketch, "E41", {"start": v(96.84, 57.15) * mm, "end": v(112.71, 57.15) * mm});
            skCircle(sketch, "E42", {"center": v(104.78, 57.15) * mm, "radius": 2 * mm});
            skSolve(sketch);
        }
        {
            var Q0;
            Q0=makeQuery(id+"F22.boolean.opBoolean","COPY",FACE,{"derivedFrom":makeQuery(id+"F22.opExtrude","CAP_FACE",FACE,{"disambiguationData":[OSD([sQuery(id+"F21.wireOp",EDGE,"E36.bottom"),sQuery(id+"F21.wireOp",EDGE,"E36.top"),sQuery(id+"F21.wireOp",EDGE,"E36.left"),sQuery(id+"F21.wireOp",EDGE,"E36.right")])],"isStart":false})});
            var sketch = newSketch(context, id + "F27", { "sketchPlane" : qUnion([Q0])});
            skLineSegment(sketch, "E43", {"start": v(-112.71, 57.15) * mm, "end": v(-96.84, 57.15) * mm});
            skCircle(sketch, "E44", {"center": v(-104.78, 57.15) * mm, "radius": 2 * mm});
            skSolve(sketch);
        }
        {
            var Q0;
            Q0 = qSketchRegion(id + "F27", true);
            var Q1;
            Q1 = qSketchRegion(id + "F26", true);
            extrude(context, id + "F28", {"entities" : qUnion([Q0, Q1]), "operationType" : NewBodyOperationType.REMOVE, "oppositeDirection" : true, "depth" : 25.4 * mm});
        }
        {
            var Q0;
            Q0=makeQuery(id+"F19.boolean.opBoolean","COPY",FACE,{"derivedFrom":makeQuery(id+"F19.opExtrude","CAP_FACE",FACE,{"disambiguationData":[OSD([sQuery(id+"F17.wireOp",EDGE,"E30.bottom"),sQuery(id+"F17.wireOp",EDGE,"E30.top"),sQuery(id+"F17.wireOp",EDGE,"E30.left"),sQuery(id+"F17.wireOp",EDGE,"E30.right")])],"isStart":false})});
            var sketch = newSketch(context, id + "F29", { "sketchPlane" : qUnion([Q0])});
            skLineSegment(sketch, "E45", {"start": v(96.84, -57.15) * mm, "end": v(112.71, -57.15) * mm});
            skCircle(sketch, "E46.cCircle", {"center": v(104.77, -57.15) * mm, "radius": 5.56 * mm, "construction": true});
            skLineSegment(sketch, "E46.0", {"start": v(110.33, -57.15) * mm, "end": v(107.55, -61.96) * mm});
            skLineSegment(sketch, "E46.1", {"start": v(107.55, -61.96) * mm, "end": v(102, -61.96) * mm});
            skLineSegment(sketch, "E46.2", {"start": v(102, -61.96) * mm, "end": v(99.22, -57.15) * mm});
            skLineSegment(sketch, "E46.3", {"start": v(99.22, -57.15) * mm, "end": v(102, -52.34) * mm});
            skLineSegment(sketch, "E46.4", {"start": v(102, -52.34) * mm, "end": v(107.55, -52.34) * mm});
            skLineSegment(sketch, "E46.5", {"start": v(107.55, -52.34) * mm, "end": v(110.33, -57.15) * mm});
            skSolve(sketch);
        }
        {
            var Q0;
            Q0=makeQuery(id+"F19.boolean.opBoolean","COPY",FACE,{"derivedFrom":makeQuery(id+"F19.opExtrude","CAP_FACE",FACE,{"disambiguationData":[OSD([sQuery(id+"F18.wireOp",EDGE,"E32.bottom"),sQuery(id+"F18.wireOp",EDGE,"E32.top"),sQuery(id+"F18.wireOp",EDGE,"E32.left"),sQuery(id+"F18.wireOp",EDGE,"E32.right")])],"isStart":false})});
            var sketch = newSketch(context, id + "F30", { "sketchPlane" : qUnion([Q0])});
            skCircle(sketch, "E47.cCircle", {"center": v(-104.78, -57.15) * mm, "radius": 5.56 * mm, "construction": true});
            skLineSegment(sketch, "E47.0", {"start": v(-99.22, -57.15) * mm, "end": v(-102, -61.96) * mm});
            skLineSegment(sketch, "E47.1", {"start": v(-102, -61.96) * mm, "end": v(-107.55, -61.96) * mm});
            skLineSegment(sketch, "E47.2", {"start": v(-107.55, -61.96) * mm, "end": v(-110.33, -57.15) * mm});
            skLineSegment(sketch, "E47.3", {"start": v(-110.33, -57.15) * mm, "end": v(-107.55, -52.34) * mm});
            skLineSegment(sketch, "E47.4", {"start": v(-107.55, -52.34) * mm, "end": v(-102, -52.34) * mm});
            skLineSegment(sketch, "E47.5", {"start": v(-102, -52.34) * mm, "end": v(-99.22, -57.15) * mm});
            skLineSegment(sketch, "E48", {"start": v(-112.71, -57.15) * mm, "end": v(-96.84, -57.15) * mm});
            skSolve(sketch);
        }
        {
            var Q0;
            Q0 = qSketchRegion(id + "F29", true);
            var Q1;
            Q1 = qSketchRegion(id + "F30", true);
            extrude(context, id + "F31", {"entities" : qUnion([Q0, Q1]), "operationType" : NewBodyOperationType.REMOVE, "oppositeDirection" : true, "depth" : 3.17 * mm});
        }
        {
            var Q0;
            Q0=makeQuery(id+"F22.boolean.opBoolean","COPY",FACE,{"derivedFrom":makeQuery(id+"F22.opExtrude","CAP_FACE",FACE,{"disambiguationData":[OSD([sQuery(id+"F21.wireOp",EDGE,"E36.bottom"),sQuery(id+"F21.wireOp",EDGE,"E36.top"),sQuery(id+"F21.wireOp",EDGE,"E36.left"),sQuery(id+"F21.wireOp",EDGE,"E36.right")])],"isStart":false})});
            var sketch = newSketch(context, id + "F32", { "sketchPlane" : qUnion([Q0])});
            skCircle(sketch, "E49.cCircle", {"center": v(-104.78, 57.15) * mm, "radius": 5.56 * mm, "construction": true});
            skLineSegment(sketch, "E49.0", {"start": v(-99.22, 57.15) * mm, "end": v(-102, 52.34) * mm});
            skLineSegment(sketch, "E49.1", {"start": v(-102, 52.34) * mm, "end": v(-107.55, 52.34) * mm});
            skLineSegment(sketch, "E49.2", {"start": v(-107.55, 52.34) * mm, "end": v(-110.33, 57.15) * mm});
            skLineSegment(sketch, "E49.3", {"start": v(-110.33, 57.15) * mm, "end": v(-107.55, 61.96) * mm});
            skLineSegment(sketch, "E49.4", {"start": v(-107.55, 61.96) * mm, "end": v(-102, 61.96) * mm});
            skLineSegment(sketch, "E49.5", {"start": v(-102, 61.96) * mm, "end": v(-99.22, 57.15) * mm});
            skLineSegment(sketch, "E50", {"start": v(-112.71, 57.15) * mm, "end": v(-96.84, 57.15) * mm});
            skSolve(sketch);
        }
        {
            var Q0;
            Q0=makeQuery(id+"F22.boolean.opBoolean","COPY",FACE,{"derivedFrom":makeQuery(id+"F22.opExtrude","CAP_FACE",FACE,{"disambiguationData":[OSD([sQuery(id+"F20.wireOp",EDGE,"E34.bottom"),sQuery(id+"F20.wireOp",EDGE,"E34.top"),sQuery(id+"F20.wireOp",EDGE,"E34.left"),sQuery(id+"F20.wireOp",EDGE,"E34.right")])],"isStart":false})});
            var sketch = newSketch(context, id + "F33", { "sketchPlane" : qUnion([Q0])});
            skCircle(sketch, "E51.cCircle", {"center": v(104.78, 57.15) * mm, "radius": 5.56 * mm, "construction": true});
            skLineSegment(sketch, "E51.0", {"start": v(110.33, 57.15) * mm, "end": v(107.55, 52.34) * mm});
            skLineSegment(sketch, "E51.1", {"start": v(107.55, 52.34) * mm, "end": v(102, 52.34) * mm});
            skLineSegment(sketch, "E51.2", {"start": v(102, 52.34) * mm, "end": v(99.22, 57.15) * mm});
            skLineSegment(sketch, "E51.3", {"start": v(99.22, 57.15) * mm, "end": v(102, 61.96) * mm});
            skLineSegment(sketch, "E51.4", {"start": v(102, 61.96) * mm, "end": v(107.55, 61.96) * mm});
            skLineSegment(sketch, "E51.5", {"start": v(107.55, 61.96) * mm, "end": v(110.33, 57.15) * mm});
            skLineSegment(sketch, "E52", {"start": v(96.84, 57.15) * mm, "end": v(112.71, 57.15) * mm});
            skSolve(sketch);
        }
        {
            var Q0;
            Q0 = qSketchRegion(id + "F32", true);
            var Q1;
            Q1 = qSketchRegion(id + "F33", true);
            extrude(context, id + "F34", {"entities" : qUnion([Q0, Q1]), "operationType" : NewBodyOperationType.REMOVE, "oppositeDirection" : true, "depth" : 3.17 * mm});
        }
        {
            var Q0;
            Q0=makeQuery(id+"F19.boolean.opBoolean","COPY",FACE,{"derivedFrom":makeQuery(id+"F19.opExtrude","CAP_FACE",FACE,{"disambiguationData":[OSD([sQuery(id+"F17.wireOp",EDGE,"E30.bottom"),sQuery(id+"F17.wireOp",EDGE,"E30.top"),sQuery(id+"F17.wireOp",EDGE,"E30.left"),sQuery(id+"F17.wireOp",EDGE,"E30.right")])],"isStart":false})});
            var sketch = newSketch(context, id + "F35", { "sketchPlane" : qUnion([Q0])});
            skLineSegment(sketch, "E53.bottom", {"start": v(96.84, -49.21) * mm, "end": v(112.71, -49.21) * mm});
            skLineSegment(sketch, "E53.top", {"start": v(96.84, -65.09) * mm, "end": v(112.71, -65.09) * mm});
            skLineSegment(sketch, "E53.left", {"start": v(96.84, -49.21) * mm, "end": v(96.84, -65.09) * mm});
            skLineSegment(sketch, "E53.right", {"start": v(112.71, -49.21) * mm, "end": v(112.71, -65.09) * mm});
            skSolve(sketch);
        }
        {
            var Q0;
            Q0=makeQuery(id+"F19.boolean.opBoolean","COPY",FACE,{"derivedFrom":makeQuery(id+"F19.opExtrude","CAP_FACE",FACE,{"disambiguationData":[OSD([sQuery(id+"F18.wireOp",EDGE,"E32.bottom"),sQuery(id+"F18.wireOp",EDGE,"E32.top"),sQuery(id+"F18.wireOp",EDGE,"E32.left"),sQuery(id+"F18.wireOp",EDGE,"E32.right")])],"isStart":false})});
            var sketch = newSketch(context, id + "F36", { "sketchPlane" : qUnion([Q0])});
            skLineSegment(sketch, "E54.bottom", {"start": v(-112.71, -49.21) * mm, "end": v(-96.84, -49.21) * mm});
            skLineSegment(sketch, "E54.top", {"start": v(-112.71, -65.09) * mm, "end": v(-96.84, -65.09) * mm});
            skLineSegment(sketch, "E54.left", {"start": v(-112.71, -49.21) * mm, "end": v(-112.71, -65.09) * mm});
            skLineSegment(sketch, "E54.right", {"start": v(-96.84, -49.21) * mm, "end": v(-96.84, -65.09) * mm});
            skSolve(sketch);
        }
        {
            var Q0;
            Q0 = qSketchRegion(id + "F35", true);
            var Q1;
            Q1 = qSketchRegion(id + "F36", true);
            extrude(context, id + "F37", {"entities" : qUnion([Q0, Q1]), "depth" : 38.1 * mm});
        }
        {
            var Q0;
            Q0=makeQuery(id+"F22.boolean.opBoolean","COPY",FACE,{"derivedFrom":makeQuery(id+"F22.opExtrude","CAP_FACE",FACE,{"disambiguationData":[OSD([sQuery(id+"F21.wireOp",EDGE,"E36.bottom"),sQuery(id+"F21.wireOp",EDGE,"E36.top"),sQuery(id+"F21.wireOp",EDGE,"E36.left"),sQuery(id+"F21.wireOp",EDGE,"E36.right")])],"isStart":false})});
            var sketch = newSketch(context, id + "F38", { "sketchPlane" : qUnion([Q0])});
            skLineSegment(sketch, "E55.bottom", {"start": v(-112.71, 65.09) * mm, "end": v(-96.84, 65.09) * mm});
            skLineSegment(sketch, "E55.top", {"start": v(-112.71, 49.21) * mm, "end": v(-96.84, 49.21) * mm});
            skLineSegment(sketch, "E55.left", {"start": v(-112.71, 65.09) * mm, "end": v(-112.71, 49.21) * mm});
            skLineSegment(sketch, "E55.right", {"start": v(-96.84, 65.09) * mm, "end": v(-96.84, 49.21) * mm});
            skSolve(sketch);
        }
        {
            var Q0;
            Q0=makeQuery(id+"F22.boolean.opBoolean","COPY",FACE,{"derivedFrom":makeQuery(id+"F22.opExtrude","CAP_FACE",FACE,{"disambiguationData":[OSD([sQuery(id+"F20.wireOp",EDGE,"E34.bottom"),sQuery(id+"F20.wireOp",EDGE,"E34.top"),sQuery(id+"F20.wireOp",EDGE,"E34.left"),sQuery(id+"F20.wireOp",EDGE,"E34.right")])],"isStart":false})});
            var sketch = newSketch(context, id + "F39", { "sketchPlane" : qUnion([Q0])});
            skLineSegment(sketch, "E56.bottom", {"start": v(96.84, 65.09) * mm, "end": v(112.71, 65.09) * mm});
            skLineSegment(sketch, "E56.top", {"start": v(96.84, 49.21) * mm, "end": v(112.71, 49.21) * mm});
            skLineSegment(sketch, "E56.left", {"start": v(96.84, 65.09) * mm, "end": v(96.84, 49.21) * mm});
            skLineSegment(sketch, "E56.right", {"start": v(112.71, 65.09) * mm, "end": v(112.71, 49.21) * mm});
            skSolve(sketch);
        }
        {
            var Q0;
            Q0 = qSketchRegion(id + "F39", true);
            var Q1;
            Q1 = qSketchRegion(id + "F38", true);
            extrude(context, id + "F40", {"entities" : qUnion([Q0, Q1]), "depth" : 38.1 * mm});
        }
        {
            var Q0;
            Q0=makeQuery(id+"F37.opExtrude","SWEPT_FACE",FACE,{"disambiguationData":[OSD([sQuery(id+"F35.wireOp",EDGE,"E53.top")])]});
            var sketch = newSketch(context, id + "F41", { "sketchPlane" : qUnion([Q0])});
            skLineSegment(sketch, "E57.bottom", {"start": v(96.84, 139.7) * mm, "end": v(112.71, 139.7) * mm});
            skLineSegment(sketch, "E57.top", {"start": v(96.84, 123.82) * mm, "end": v(112.71, 123.82) * mm});
            skLineSegment(sketch, "E57.left", {"start": v(96.84, 139.7) * mm, "end": v(96.84, 123.82) * mm});
            skLineSegment(sketch, "E57.right", {"start": v(112.71, 139.7) * mm, "end": v(112.71, 123.82) * mm});
            skSolve(sketch);
        }
        {
            var Q0;
            Q0=makeQuery(id+"F37.opExtrude","SWEPT_FACE",FACE,{"disambiguationData":[OSD([sQuery(id+"F36.wireOp",EDGE,"E54.top")])]});
            var sketch = newSketch(context, id + "F42", { "sketchPlane" : qUnion([Q0])});
            skLineSegment(sketch, "E58.bottom", {"start": v(-112.71, 139.7) * mm, "end": v(-96.84, 139.7) * mm});
            skLineSegment(sketch, "E58.top", {"start": v(-112.71, 123.82) * mm, "end": v(-96.84, 123.82) * mm});
            skLineSegment(sketch, "E58.left", {"start": v(-112.71, 139.7) * mm, "end": v(-112.71, 123.82) * mm});
            skLineSegment(sketch, "E58.right", {"start": v(-96.84, 139.7) * mm, "end": v(-96.84, 123.82) * mm});
            skSolve(sketch);
        }
        {
            var Q0;
            Q0=makeQuery(id+"F40.opExtrude","SWEPT_FACE",FACE,{"disambiguationData":[OSD([sQuery(id+"F39.wireOp",EDGE,"E56.bottom")])]});
            var sketch = newSketch(context, id + "F43", { "sketchPlane" : qUnion([Q0])});
            skLineSegment(sketch, "E59.bottom", {"start": v(96.84, -139.7) * mm, "end": v(112.71, -139.7) * mm});
            skLineSegment(sketch, "E59.top", {"start": v(96.84, -123.82) * mm, "end": v(112.71, -123.82) * mm});
            skLineSegment(sketch, "E59.left", {"start": v(96.84, -139.7) * mm, "end": v(96.84, -123.82) * mm});
            skLineSegment(sketch, "E59.right", {"start": v(112.71, -139.7) * mm, "end": v(112.71, -123.82) * mm});
            skSolve(sketch);
        }
        {
            var Q0;
            Q0=makeQuery(id+"F40.opExtrude","SWEPT_FACE",FACE,{"disambiguationData":[OSD([sQuery(id+"F38.wireOp",EDGE,"E55.bottom")])]});
            var sketch = newSketch(context, id + "F44", { "sketchPlane" : qUnion([Q0])});
            skLineSegment(sketch, "E60.bottom", {"start": v(-112.71, -139.7) * mm, "end": v(-96.84, -139.7) * mm});
            skLineSegment(sketch, "E60.top", {"start": v(-112.71, -123.82) * mm, "end": v(-96.84, -123.82) * mm});
            skLineSegment(sketch, "E60.left", {"start": v(-112.71, -139.7) * mm, "end": v(-112.71, -123.83) * mm});
            skLineSegment(sketch, "E60.right", {"start": v(-96.84, -139.7) * mm, "end": v(-96.84, -123.82) * mm});
            skSolve(sketch);
        }
        {
            var Q0;
            Q0 = qSketchRegion(id + "F44", true);
            var Q1;
            Q1 = qSketchRegion(id + "F43", true);
            var Q2;
            Q2 = qSketchRegion(id + "F42", true);
            var Q3;
            Q3 = qSketchRegion(id + "F41", true);
            extrude(context, id + "F45", {"entities" : qUnion([Q0, Q1, Q2, Q3]), "operationType" : NewBodyOperationType.ADD, "depth" : 60.32 * mm});
        }
        {
            var Q0;
            Q0=makeQuery(id+"F45.boolean.opBoolean","MERGE",FACE,{"derivedFrom":[makeQuery(id+"F37.opExtrude","SWEPT_FACE",FACE,{"disambiguationData":[OSD([sQuery(id+"F35.wireOp",EDGE,"E53.right")])]}),makeQuery(id+"F45.opExtrude","SWEPT_FACE",FACE,{"disambiguationData":[OSD([sQuery(id+"F41.wireOp",EDGE,"E57.right")])]})]});
            var sketch = newSketch(context, id + "F46", { "sketchPlane" : qUnion([Q0])});
            skLineSegment(sketch, "E61", {"start": v(-49.21, 139.7) * mm, "end": v(-58.74, 139.7) * mm});
            skLineSegment(sketch, "E62", {"start": v(-49.21, 139.7) * mm, "end": v(-49.21, 130.17) * mm});
            skPoint(sketch, "E63", {"position": v(-58.74, 130.17) * mm});
            skCircle(sketch, "E64", {"center": v(-58.74, 130.17) * mm, "radius": 6.35 * mm});
            skSolve(sketch);
        }
        {
            var Q0;
            Q0=makeQuery(id+"F45.boolean.opBoolean","MERGE",FACE,{"derivedFrom":[makeQuery(id+"F40.opExtrude","SWEPT_FACE",FACE,{"disambiguationData":[OSD([sQuery(id+"F39.wireOp",EDGE,"E56.right")])]}),makeQuery(id+"F45.opExtrude","SWEPT_FACE",FACE,{"disambiguationData":[OSD([sQuery(id+"F43.wireOp",EDGE,"E59.right")])]})]});
            var sketch = newSketch(context, id + "F47", { "sketchPlane" : qUnion([Q0])});
            skPoint(sketch, "E65", {"position": v(-58.74, -130.17) * mm});
            skCircle(sketch, "E66", {"center": v(-58.74, -130.17) * mm, "radius": 6.35 * mm});
            skSolve(sketch);
        }
        {
            var Q0;
            Q0 = qSketchRegion(id + "F46", true);
            var Q1;
            Q1 = qSketchRegion(id + "F47", true);
            extrude(context, id + "F48", {"entities" : qUnion([Q0, Q1]), "operationType" : NewBodyOperationType.ADD, "depth" : 3.17 * mm});
        }
        {
            var Q0;
            Q0=makeQuery(id+"F45.boolean.opBoolean","MERGE",FACE,{"derivedFrom":[makeQuery(id+"F37.opExtrude","SWEPT_FACE",FACE,{"disambiguationData":[OSD([sQuery(id+"F36.wireOp",EDGE,"E54.left")])]}),makeQuery(id+"F45.opExtrude","SWEPT_FACE",FACE,{"disambiguationData":[OSD([sQuery(id+"F42.wireOp",EDGE,"E58.left")])]})]});
            var sketch = newSketch(context, id + "F49", { "sketchPlane" : qUnion([Q0])});
            skPoint(sketch, "E67", {"position": v(58.74, 130.17) * mm});
            skCircle(sketch, "E68", {"center": v(58.74, 130.17) * mm, "radius": 6.35 * mm});
            skSolve(sketch);
        }
        {
            var Q0;
            Q0=makeQuery(id+"F45.boolean.opBoolean","MERGE",FACE,{"derivedFrom":[makeQuery(id+"F40.opExtrude","SWEPT_FACE",FACE,{"disambiguationData":[OSD([sQuery(id+"F38.wireOp",EDGE,"E55.left")])]}),makeQuery(id+"F45.opExtrude","SWEPT_FACE",FACE,{"disambiguationData":[OSD([sQuery(id+"F44.wireOp",EDGE,"E60.left")])]})]});
            var sketch = newSketch(context, id + "F50", { "sketchPlane" : qUnion([Q0])});
            skPoint(sketch, "E69", {"position": v(58.74, -130.17) * mm});
            skCircle(sketch, "E70", {"center": v(58.74, -130.17) * mm, "radius": 6.35 * mm});
            skSolve(sketch);
        }
        {
            var Q0;
            Q0 = qSketchRegion(id + "F50", true);
            var Q1;
            Q1 = qSketchRegion(id + "F49", true);
            extrude(context, id + "F51", {"entities" : qUnion([Q0, Q1]), "operationType" : NewBodyOperationType.ADD, "depth" : 3.17 * mm});
        }
        {
            var Q0;
            Q0=makeQuery(id+"F45.boolean.opBoolean","MERGE",FACE,{"derivedFrom":[makeQuery(id+"F37.opExtrude","SWEPT_FACE",FACE,{"disambiguationData":[OSD([sQuery(id+"F35.wireOp",EDGE,"E53.right")])]}),makeQuery(id+"F45.opExtrude","SWEPT_FACE",FACE,{"disambiguationData":[OSD([sQuery(id+"F41.wireOp",EDGE,"E57.right")])]})]});
            var sketch = newSketch(context, id + "F52", { "sketchPlane" : qUnion([Q0])});
            skPoint(sketch, "E71", {"position": v(-115.89, 131.76) * mm});
            skPoint(sketch, "E71.positionSnap0", {"position": v(-125.41, 131.76) * mm});
            skLineSegment(sketch, "E72.bottom", {"start": v(-123.82, 138.11) * mm, "end": v(-107.95, 138.11) * mm});
            skLineSegment(sketch, "E72.top", {"start": v(-123.82, 125.41) * mm, "end": v(-107.95, 125.41) * mm});
            skLineSegment(sketch, "E72.left", {"start": v(-123.82, 138.11) * mm, "end": v(-123.82, 125.41) * mm});
            skLineSegment(sketch, "E72.right", {"start": v(-107.95, 138.11) * mm, "end": v(-107.95, 125.41) * mm});
            skSolve(sketch);
        }
        {
            var Q0;
            Q0=makeQuery(id+"F45.boolean.opBoolean","MERGE",FACE,{"derivedFrom":[makeQuery(id+"F40.opExtrude","SWEPT_FACE",FACE,{"disambiguationData":[OSD([sQuery(id+"F39.wireOp",EDGE,"E56.right")])]}),makeQuery(id+"F45.opExtrude","SWEPT_FACE",FACE,{"disambiguationData":[OSD([sQuery(id+"F43.wireOp",EDGE,"E59.right")])]})]});
            var sketch = newSketch(context, id + "F53", { "sketchPlane" : qUnion([Q0])});
            skPoint(sketch, "E73", {"position": v(-115.89, -131.76) * mm});
            skPoint(sketch, "E73.positionSnap0", {"position": v(-125.41, -131.76) * mm});
            skLineSegment(sketch, "E74.bottom", {"start": v(-107.95, -125.41) * mm, "end": v(-123.82, -125.41) * mm});
            skLineSegment(sketch, "E74.top", {"start": v(-107.95, -138.11) * mm, "end": v(-123.82, -138.11) * mm});
            skLineSegment(sketch, "E74.left", {"start": v(-107.95, -125.41) * mm, "end": v(-107.95, -138.11) * mm});
            skLineSegment(sketch, "E74.right", {"start": v(-123.82, -125.41) * mm, "end": v(-123.82, -138.11) * mm});
            skSolve(sketch);
        }
        {
            var Q0;
            Q0 = qSketchRegion(id + "F53", true);
            var Q1;
            Q1 = qSketchRegion(id + "F52", true);
            extrude(context, id + "F54", {"entities" : qUnion([Q0, Q1]), "operationType" : NewBodyOperationType.ADD, "depth" : 25.4 * mm});
        }
        {
            var Q0;
            Q0=makeQuery(id+"F45.boolean.opBoolean","MERGE",FACE,{"derivedFrom":[makeQuery(id+"F37.opExtrude","SWEPT_FACE",FACE,{"disambiguationData":[OSD([sQuery(id+"F36.wireOp",EDGE,"E54.left")])]}),makeQuery(id+"F45.opExtrude","SWEPT_FACE",FACE,{"disambiguationData":[OSD([sQuery(id+"F42.wireOp",EDGE,"E58.left")])]})]});
            var sketch = newSketch(context, id + "F55", { "sketchPlane" : qUnion([Q0])});
            skPoint(sketch, "E75", {"position": v(115.89, 131.76) * mm});
            skPoint(sketch, "E75.positionSnap0", {"position": v(125.41, 131.76) * mm});
            skLineSegment(sketch, "E76.bottom", {"start": v(123.83, 138.11) * mm, "end": v(107.95, 138.11) * mm});
            skLineSegment(sketch, "E76.top", {"start": v(123.83, 125.41) * mm, "end": v(107.95, 125.41) * mm});
            skLineSegment(sketch, "E76.left", {"start": v(123.83, 138.11) * mm, "end": v(123.83, 125.41) * mm});
            skLineSegment(sketch, "E76.right", {"start": v(107.95, 138.11) * mm, "end": v(107.95, 125.41) * mm});
            skPoint(sketch, "E77.orphan", {"position": v(125.41, 123.82) * mm});
            skPoint(sketch, "E78.left.end.orphan", {"position": v(125.41, 139.7) * mm});
            skSolve(sketch);
        }
        {
            var Q0;
            Q0=makeQuery(id+"F45.boolean.opBoolean","MERGE",FACE,{"derivedFrom":[makeQuery(id+"F40.opExtrude","SWEPT_FACE",FACE,{"disambiguationData":[OSD([sQuery(id+"F38.wireOp",EDGE,"E55.left")])]}),makeQuery(id+"F45.opExtrude","SWEPT_FACE",FACE,{"disambiguationData":[OSD([sQuery(id+"F44.wireOp",EDGE,"E60.left")])]})]});
            var sketch = newSketch(context, id + "F56", { "sketchPlane" : qUnion([Q0])});
            skPoint(sketch, "E79", {"position": v(115.89, -131.76) * mm});
            skPoint(sketch, "E79.positionSnap0", {"position": v(125.41, -131.76) * mm});
            skLineSegment(sketch, "E80.bottom", {"start": v(123.82, -125.41) * mm, "end": v(107.95, -125.41) * mm});
            skLineSegment(sketch, "E80.top", {"start": v(123.82, -138.11) * mm, "end": v(107.95, -138.11) * mm});
            skLineSegment(sketch, "E80.left", {"start": v(123.82, -125.41) * mm, "end": v(123.82, -138.11) * mm});
            skLineSegment(sketch, "E80.right", {"start": v(107.95, -125.41) * mm, "end": v(107.95, -138.11) * mm});
            skSolve(sketch);
        }
        {
            var Q0;
            Q0 = qSketchRegion(id + "F56", true);
            var Q1;
            Q1 = qSketchRegion(id + "F55", true);
            extrude(context, id + "F57", {"entities" : qUnion([Q0, Q1]), "operationType" : NewBodyOperationType.ADD, "depth" : 25.4 * mm});
        }
        {
            var Q0;
            Q0=makeQuery(id+"F45.boolean.opBoolean","MERGE",FACE,{"derivedFrom":[makeQuery(id+"F37.opExtrude","SWEPT_FACE",FACE,{"disambiguationData":[OSD([sQuery(id+"F36.wireOp",EDGE,"E54.right")])]}),makeQuery(id+"F45.opExtrude","SWEPT_FACE",FACE,{"disambiguationData":[OSD([sQuery(id+"F42.wireOp",EDGE,"E58.right")])]})]});
            var sketch = newSketch(context, id + "F58", { "sketchPlane" : qUnion([Q0])});
            skPoint(sketch, "E81", {"position": v(-117.48, 131.76) * mm});
            skPoint(sketch, "E81.positionSnap0", {"position": v(-125.41, 131.76) * mm});
            skCircle(sketch, "E82", {"center": v(-117.48, 131.76) * mm, "radius": 6.35 * mm});
            skSolve(sketch);
        }
        {
            var Q0;
            Q0=makeQuery(id+"F45.boolean.opBoolean","MERGE",FACE,{"derivedFrom":[makeQuery(id+"F40.opExtrude","SWEPT_FACE",FACE,{"disambiguationData":[OSD([sQuery(id+"F38.wireOp",EDGE,"E55.right")])]}),makeQuery(id+"F45.opExtrude","SWEPT_FACE",FACE,{"disambiguationData":[OSD([sQuery(id+"F44.wireOp",EDGE,"E60.right")])]})]});
            var sketch = newSketch(context, id + "F59", { "sketchPlane" : qUnion([Q0])});
            skPoint(sketch, "E83", {"position": v(-117.47, -131.76) * mm});
            skPoint(sketch, "E83.positionSnap0", {"position": v(-125.41, -131.76) * mm});
            skCircle(sketch, "E84", {"center": v(-117.5, -131.76) * mm, "radius": 6.35 * mm});
            skSolve(sketch);
        }
        {
            var Q0;
            Q0 = qSketchRegion(id + "F59", true);
            var Q1;
            Q1 = qSketchRegion(id + "F58", true);
            extrude(context, id + "F60", {"entities" : qUnion([Q0, Q1]), "operationType" : NewBodyOperationType.ADD, "depth" : 3.17 * mm});
        }
        {
            var Q0;
            Q0=makeQuery(id+"F45.boolean.opBoolean","MERGE",FACE,{"derivedFrom":[makeQuery(id+"F37.opExtrude","SWEPT_FACE",FACE,{"disambiguationData":[OSD([sQuery(id+"F35.wireOp",EDGE,"E53.left")])]}),makeQuery(id+"F45.opExtrude","SWEPT_FACE",FACE,{"disambiguationData":[OSD([sQuery(id+"F41.wireOp",EDGE,"E57.left")])]})]});
            var sketch = newSketch(context, id + "F61", { "sketchPlane" : qUnion([Q0])});
            skPoint(sketch, "E85", {"position": v(117.47, 131.76) * mm});
            skPoint(sketch, "E85.positionSnap0", {"position": v(125.41, 131.76) * mm});
            skCircle(sketch, "E86", {"center": v(117.47, 131.76) * mm, "radius": 6.35 * mm});
            skSolve(sketch);
        }
        {
            var Q0;
            Q0=makeQuery(id+"F45.boolean.opBoolean","MERGE",FACE,{"derivedFrom":[makeQuery(id+"F40.opExtrude","SWEPT_FACE",FACE,{"disambiguationData":[OSD([sQuery(id+"F39.wireOp",EDGE,"E56.left")])]}),makeQuery(id+"F45.opExtrude","SWEPT_FACE",FACE,{"disambiguationData":[OSD([sQuery(id+"F43.wireOp",EDGE,"E59.left")])]})]});
            var sketch = newSketch(context, id + "F62", { "sketchPlane" : qUnion([Q0])});
            skPoint(sketch, "E87", {"position": v(117.47, -131.76) * mm});
            skPoint(sketch, "E87.positionSnap0", {"position": v(125.41, -131.76) * mm});
            skCircle(sketch, "E88", {"center": v(117.47, -131.76) * mm, "radius": 6.35 * mm});
            skSolve(sketch);
        }
        {
            var Q0;
            Q0 = qSketchRegion(id + "F62", true);
            var Q1;
            Q1 = qSketchRegion(id + "F61", true);
            extrude(context, id + "F63", {"entities" : qUnion([Q0, Q1]), "operationType" : NewBodyOperationType.ADD, "depth" : 3.17 * mm});
        }
        {
            var Q0;
            Q0=makeQuery(id+"F54.opExtrude","SWEPT_FACE",FACE,{"disambiguationData":[OSD([sQuery(id+"F52.wireOp",EDGE,"E72.bottom")])]});
            var sketch = newSketch(context, id + "F64", { "sketchPlane" : qUnion([Q0])});
            skLineSegment(sketch, "E89.bottom", {"start": v(138.11, -107.95) * mm, "end": v(125.41, -107.95) * mm});
            skLineSegment(sketch, "E89.top", {"start": v(138.11, -123.82) * mm, "end": v(125.41, -123.82) * mm});
            skLineSegment(sketch, "E89.left", {"start": v(138.11, -107.95) * mm, "end": v(138.11, -123.82) * mm});
            skLineSegment(sketch, "E89.right", {"start": v(125.41, -107.95) * mm, "end": v(125.41, -123.82) * mm});
            skSolve(sketch);
        }
        {
            var Q0;
            Q0=makeQuery(id+"F57.opExtrude","SWEPT_FACE",FACE,{"disambiguationData":[OSD([sQuery(id+"F55.wireOp",EDGE,"E76.bottom")])]});
            var sketch = newSketch(context, id + "F65", { "sketchPlane" : qUnion([Q0])});
            skLineSegment(sketch, "E90.bottom", {"start": v(-138.11, -107.95) * mm, "end": v(-125.41, -107.95) * mm});
            skLineSegment(sketch, "E90.top", {"start": v(-138.11, -123.83) * mm, "end": v(-125.41, -123.83) * mm});
            skLineSegment(sketch, "E90.left", {"start": v(-138.11, -107.95) * mm, "end": v(-138.11, -123.83) * mm});
            skLineSegment(sketch, "E90.right", {"start": v(-125.41, -107.95) * mm, "end": v(-125.41, -123.83) * mm});
            skSolve(sketch);
        }
        {
            var Q0;
            Q0 = qSketchRegion(id + "F65", true);
            var Q1;
            Q1 = qSketchRegion(id + "F64", true);
            extrude(context, id + "F66", {"entities" : qUnion([Q0, Q1]), "operationType" : NewBodyOperationType.ADD, "depth" : 25.4 * mm});
        }
        {
            var Q0;
            Q0=makeQuery(id+"F54.opExtrude","SWEPT_FACE",FACE,{"disambiguationData":[OSD([sQuery(id+"F53.wireOp",EDGE,"E74.top")])]});
            var sketch = newSketch(context, id + "F67", { "sketchPlane" : qUnion([Q0])});
            skLineSegment(sketch, "E91.bottom", {"start": v(138.11, 123.82) * mm, "end": v(125.41, 123.82) * mm});
            skLineSegment(sketch, "E91.top", {"start": v(138.11, 107.95) * mm, "end": v(125.41, 107.95) * mm});
            skLineSegment(sketch, "E91.left", {"start": v(138.11, 123.82) * mm, "end": v(138.11, 107.95) * mm});
            skLineSegment(sketch, "E91.right", {"start": v(125.41, 123.82) * mm, "end": v(125.41, 107.95) * mm});
            skSolve(sketch);
        }
        {
            var Q0;
            Q0=makeQuery(id+"F57.opExtrude","SWEPT_FACE",FACE,{"disambiguationData":[OSD([sQuery(id+"F56.wireOp",EDGE,"E80.top")])]});
            var sketch = newSketch(context, id + "F68", { "sketchPlane" : qUnion([Q0])});
            skLineSegment(sketch, "E92.bottom", {"start": v(-138.11, 123.82) * mm, "end": v(-125.41, 123.82) * mm});
            skLineSegment(sketch, "E92.top", {"start": v(-138.11, 107.95) * mm, "end": v(-125.41, 107.95) * mm});
            skLineSegment(sketch, "E92.left", {"start": v(-138.11, 123.82) * mm, "end": v(-138.11, 107.95) * mm});
            skLineSegment(sketch, "E92.right", {"start": v(-125.41, 123.82) * mm, "end": v(-125.41, 107.95) * mm});
            skSolve(sketch);
        }
        {
            var Q0;
            Q0 = qSketchRegion(id + "F68", true);
            var Q1;
            Q1 = qSketchRegion(id + "F67", true);
            extrude(context, id + "F69", {"entities" : qUnion([Q0, Q1]), "operationType" : NewBodyOperationType.ADD, "depth" : 25.4 * mm});
        }
        {
            var Q0;
            Q0=makeQuery(id+"F66.opExtrude","SWEPT_FACE",FACE,{"disambiguationData":[OSD([sQuery(id+"F65.wireOp",EDGE,"E90.right")])]});
            var sketch = newSketch(context, id + "F70", { "sketchPlane" : qUnion([Q0])});
            skPoint(sketch, "E93", {"position": v(-115.89, 155.58) * mm});
            skPoint(sketch, "E93.positionSnap0", {"position": v(-115.89, 163.51) * mm});
            skCircle(sketch, "E94", {"center": v(-115.89, 155.58) * mm, "radius": 5.56 * mm});
            skSolve(sketch);
        }
        {
            var Q0;
            Q0=makeQuery(id+"F69.opExtrude","SWEPT_FACE",FACE,{"disambiguationData":[OSD([sQuery(id+"F68.wireOp",EDGE,"E92.right")])]});
            var sketch = newSketch(context, id + "F71", { "sketchPlane" : qUnion([Q0])});
            skPoint(sketch, "E95", {"position": v(-115.89, -155.58) * mm});
            skPoint(sketch, "E95.positionSnap0", {"position": v(-115.89, -163.51) * mm});
            skCircle(sketch, "E96", {"center": v(-115.89, -155.58) * mm, "radius": 5.56 * mm});
            skSolve(sketch);
        }
        {
            var Q0;
            Q0 = qSketchRegion(id + "F71", true);
            var Q1;
            Q1 = qSketchRegion(id + "F70", true);
            extrude(context, id + "F72", {"entities" : qUnion([Q0, Q1]), "operationType" : NewBodyOperationType.ADD, "depth" : 19.05 * mm});
        }
        {
            var Q0;
            Q0=makeQuery(id+"F66.opExtrude","SWEPT_FACE",FACE,{"disambiguationData":[OSD([sQuery(id+"F64.wireOp",EDGE,"E89.right")])]});
            var sketch = newSketch(context, id + "F73", { "sketchPlane" : qUnion([Q0])});
            skPoint(sketch, "E97", {"position": v(115.89, 155.58) * mm});
            skPoint(sketch, "E97.positionSnap0", {"position": v(115.89, 163.51) * mm});
            skCircle(sketch, "E98", {"center": v(115.89, 155.58) * mm, "radius": 5.56 * mm});
            skSolve(sketch);
        }
        {
            var Q0;
            Q0=makeQuery(id+"F69.opExtrude","SWEPT_FACE",FACE,{"disambiguationData":[OSD([sQuery(id+"F67.wireOp",EDGE,"E91.right")])]});
            var sketch = newSketch(context, id + "F74", { "sketchPlane" : qUnion([Q0])});
            skPoint(sketch, "E99", {"position": v(115.89, -155.58) * mm});
            skPoint(sketch, "E99.positionSnap0", {"position": v(115.89, -163.51) * mm});
            skCircle(sketch, "E100", {"center": v(115.89, -155.58) * mm, "radius": 5.56 * mm});
            skSolve(sketch);
        }
        {
            var Q0;
            Q0 = qSketchRegion(id + "F74", true);
            var Q1;
            Q1 = qSketchRegion(id + "F73", true);
            extrude(context, id + "F75", {"entities" : qUnion([Q0, Q1]), "operationType" : NewBodyOperationType.ADD, "depth" : 19.05 * mm});
        }
        {
            var Q0;
            Q0=qCreatedBy(makeId("Front.planeOp"),FACE);
            cPlane(context, id + "F76", {"entities" : qUnion([Q0]), "cplaneType" : CPlaneType.OFFSET, "offset" : 115.89 * mm, "width" : 152.4 * mm, "height" : 152.4 * mm});
        }
        {
            var Q0;
            Q0=qCreatedBy(id+"F76.planeOp",FACE);
            var sketch = newSketch(context, id + "F77", { "sketchPlane" : qUnion([Q0])});
            skPoint(sketch, "E101", {"position": v(-106.36, 155.58) * mm});
            skPoint(sketch, "E102", {"position": v(106.36, 155.58) * mm});
            skPoint(sketch, "E103", {"position": v(106.36, -155.57) * mm});
            skPoint(sketch, "E104", {"position": v(-106.36, -155.58) * mm});
            skPoint(sketch, "E105", {"position": v(0, 177.8) * mm});
            skPoint(sketch, "E106", {"position": v(0, -177.8) * mm});
            skArc(sketch, "E107", {"start": v(106.36, 155.58) * mm, "mid": v(0, 177.8) * mm, "end": v(-106.36, 155.58) * mm});
            skArc(sketch, "E108", {"start": v(-106.36, -155.58) * mm, "mid": v(0, -177.8) * mm, "end": v(106.36, -155.57) * mm});
            skSolve(sketch);
        }
        {
            var Q0;
            Q0=makeQuery(id+"F72.opExtrude","CAP_FACE",FACE,{"disambiguationData":[OSD([sQuery(id+"F70.wireOp",EDGE,"E94")])],"isStart":false});
            var Q1;
            Q1=sQuery(id+"F77.wireOp",EDGE,"E107");
            sweep(context, id + "F78", {"operationType" : NewBodyOperationType.ADD, "profiles" : qUnion([Q0]), "path" : qUnion([Q1]), "keepProfileOrientation" : true});
        }
        {
            var Q0;
            Q0=makeQuery(id+"F72.opExtrude","CAP_FACE",FACE,{"disambiguationData":[OSD([sQuery(id+"F71.wireOp",EDGE,"E96")])],"isStart":false});
            var Q1;
            Q1=sQuery(id+"F77.wireOp",EDGE,"E108");
            sweep(context, id + "F79", {"operationType" : NewBodyOperationType.ADD, "profiles" : qUnion([Q0]), "path" : qUnion([Q1]), "keepProfileOrientation" : true});
        }
        {
            var Q0;
            Q0=makeQuery(id+"F66.boolean.opBoolean","MERGE",FACE,{"derivedFrom":[makeQuery(id+"F54.opExtrude","CAP_FACE",FACE,{"disambiguationData":[OSD([sQuery(id+"F52.wireOp",EDGE,"E72.bottom"),sQuery(id+"F52.wireOp",EDGE,"E72.top"),sQuery(id+"F52.wireOp",EDGE,"E72.left"),sQuery(id+"F52.wireOp",EDGE,"E72.right")])],"isStart":false}),makeQuery(id+"F66.opExtrude","SWEPT_FACE",FACE,{"disambiguationData":[OSD([sQuery(id+"F64.wireOp",EDGE,"E89.left")])]})]});
            var sketch = newSketch(context, id + "F80", { "sketchPlane" : qUnion([Q0])});
            skPoint(sketch, "E109", {"position": v(-115.89, 155.58) * mm});
            skPoint(sketch, "E109.positionSnap0", {"position": v(-115.89, 163.51) * mm});
            skCircle(sketch, "E110", {"center": v(-115.89, 155.58) * mm, "radius": 5.56 * mm});
            skSolve(sketch);
        }
        {
            var Q0;
            Q0=makeQuery(id+"F69.boolean.opBoolean","MERGE",FACE,{"derivedFrom":[makeQuery(id+"F54.opExtrude","CAP_FACE",FACE,{"disambiguationData":[OSD([sQuery(id+"F53.wireOp",EDGE,"E74.bottom"),sQuery(id+"F53.wireOp",EDGE,"E74.top"),sQuery(id+"F53.wireOp",EDGE,"E74.left"),sQuery(id+"F53.wireOp",EDGE,"E74.right")])],"isStart":false}),makeQuery(id+"F69.opExtrude","SWEPT_FACE",FACE,{"disambiguationData":[OSD([sQuery(id+"F67.wireOp",EDGE,"E91.left")])]})]});
            var sketch = newSketch(context, id + "F81", { "sketchPlane" : qUnion([Q0])});
            skPoint(sketch, "E111", {"position": v(-115.89, -155.58) * mm});
            skPoint(sketch, "E111.positionSnap0", {"position": v(-115.89, -163.51) * mm});
            skCircle(sketch, "E112", {"center": v(-115.89, -155.58) * mm, "radius": 5.56 * mm});
            skSolve(sketch);
        }
        {
            var Q0;
            Q0 = qSketchRegion(id + "F81", true);
            var Q1;
            Q1 = qSketchRegion(id + "F80", true);
            extrude(context, id + "F82", {"entities" : qUnion([Q0, Q1]), "operationType" : NewBodyOperationType.ADD, "depth" : 4.76 * mm});
        }
        {
            var Q0;
            Q0=makeQuery(id+"F66.boolean.opBoolean","MERGE",FACE,{"derivedFrom":[makeQuery(id+"F57.opExtrude","CAP_FACE",FACE,{"disambiguationData":[OSD([sQuery(id+"F55.wireOp",EDGE,"E76.bottom"),sQuery(id+"F55.wireOp",EDGE,"E76.top"),sQuery(id+"F55.wireOp",EDGE,"E76.left"),sQuery(id+"F55.wireOp",EDGE,"E76.right")])],"isStart":false}),makeQuery(id+"F66.opExtrude","SWEPT_FACE",FACE,{"disambiguationData":[OSD([sQuery(id+"F65.wireOp",EDGE,"E90.left")])]})]});
            var sketch = newSketch(context, id + "F83", { "sketchPlane" : qUnion([Q0])});
            skPoint(sketch, "E113", {"position": v(115.89, 155.58) * mm});
            skPoint(sketch, "E113.positionSnap0", {"position": v(115.89, 163.51) * mm});
            skCircle(sketch, "E114", {"center": v(115.89, 155.58) * mm, "radius": 5.56 * mm});
            skSolve(sketch);
        }
        {
            var Q0;
            Q0=makeQuery(id+"F69.boolean.opBoolean","MERGE",FACE,{"derivedFrom":[makeQuery(id+"F57.opExtrude","CAP_FACE",FACE,{"disambiguationData":[OSD([sQuery(id+"F56.wireOp",EDGE,"E80.bottom"),sQuery(id+"F56.wireOp",EDGE,"E80.top"),sQuery(id+"F56.wireOp",EDGE,"E80.left"),sQuery(id+"F56.wireOp",EDGE,"E80.right")])],"isStart":false}),makeQuery(id+"F69.opExtrude","SWEPT_FACE",FACE,{"disambiguationData":[OSD([sQuery(id+"F68.wireOp",EDGE,"E92.left")])]})]});
            var sketch = newSketch(context, id + "F84", { "sketchPlane" : qUnion([Q0])});
            skPoint(sketch, "E115", {"position": v(115.89, -155.58) * mm});
            skPoint(sketch, "E115.positionSnap0", {"position": v(115.89, -163.51) * mm});
            skCircle(sketch, "E116", {"center": v(115.89, -155.58) * mm, "radius": 5.56 * mm});
            skSolve(sketch);
        }
        {
            var Q0;
            Q0 = qSketchRegion(id + "F84", true);
            var Q1;
            Q1 = qSketchRegion(id + "F83", true);
            extrude(context, id + "F85", {"entities" : qUnion([Q0, Q1]), "operationType" : NewBodyOperationType.ADD, "depth" : 4.76 * mm});
        }
        {
            var Q0;
            Q0=makeQuery(id+"F85.opExtrude","CAP_EDGE",EDGE,{"disambiguationData":[OSD([sQuery(id+"F83.wireOp",EDGE,"E114")])],"isStart":false});
            var Q1;
            Q1=makeQuery(id+"F82.opExtrude","CAP_EDGE",EDGE,{"disambiguationData":[OSD([sQuery(id+"F80.wireOp",EDGE,"E110")])],"isStart":false});
            var Q2;
            Q2=makeQuery(id+"F82.opExtrude","CAP_EDGE",EDGE,{"disambiguationData":[OSD([sQuery(id+"F81.wireOp",EDGE,"E112")])],"isStart":false});
            var Q3;
            Q3=makeQuery(id+"F85.opExtrude","CAP_EDGE",EDGE,{"disambiguationData":[OSD([sQuery(id+"F84.wireOp",EDGE,"E116")])],"isStart":false});
            chamfer(context, id + "F86", {"entities" : qUnion([Q0, Q1, Q2, Q3]), "width" : 1.59 * mm, "tangentPropagation" : true});
        }
        {
            var Q0;
            Q0=makeQuery(id+"F45.boolean.opBoolean","MERGE",FACE,{"derivedFrom":[makeQuery(id+"F37.opExtrude","CAP_FACE",FACE,{"disambiguationData":[OSD([sQuery(id+"F35.wireOp",EDGE,"E53.bottom"),sQuery(id+"F35.wireOp",EDGE,"E53.top"),sQuery(id+"F35.wireOp",EDGE,"E53.left"),sQuery(id+"F35.wireOp",EDGE,"E53.right")])],"isStart":false}),makeQuery(id+"F45.opExtrude","SWEPT_FACE",FACE,{"disambiguationData":[OSD([sQuery(id+"F41.wireOp",EDGE,"E57.bottom")])]})]});
            var sketch = newSketch(context, id + "F87", { "sketchPlane" : qUnion([Q0])});
            skPoint(sketch, "E117", {"position": v(104.77, -57.15) * mm});
            skPoint(sketch, "E117.positionSnap0", {"position": v(104.77, -49.21) * mm});
            skSolve(sketch);
        }
        {
            var Q0;
            Q0=makeQuery(id+"F45.boolean.opBoolean","MERGE",FACE,{"derivedFrom":[makeQuery(id+"F37.opExtrude","CAP_FACE",FACE,{"disambiguationData":[OSD([sQuery(id+"F36.wireOp",EDGE,"E54.bottom"),sQuery(id+"F36.wireOp",EDGE,"E54.top"),sQuery(id+"F36.wireOp",EDGE,"E54.left"),sQuery(id+"F36.wireOp",EDGE,"E54.right")])],"isStart":false}),makeQuery(id+"F45.opExtrude","SWEPT_FACE",FACE,{"disambiguationData":[OSD([sQuery(id+"F42.wireOp",EDGE,"E58.bottom")])]})]});
            var sketch = newSketch(context, id + "F88", { "sketchPlane" : qUnion([Q0])});
            skPoint(sketch, "E118", {"position": v(-104.78, -57.15) * mm});
            skPoint(sketch, "E118.positionSnap0", {"position": v(-104.78, -49.21) * mm});
            skSolve(sketch);
        }
        {
            var Q0;
            Q0=sQuery(id+"F88.wireOp",VERTEX,"E118");
            var Q1;
            Q1=sQuery(id+"F87.wireOp",VERTEX,"E117");
            var Q2;
            Q2=makeQuery(id+"F37.opExtrude","SWEPT_BODY",BODY,{"disambiguationData":[OSD([sQuery(id+"F35.wireOp",EDGE,"E53.bottom"),sQuery(id+"F35.wireOp",EDGE,"E53.top"),sQuery(id+"F35.wireOp",EDGE,"E53.left"),sQuery(id+"F35.wireOp",EDGE,"E53.right")])]});
            hole(context, id + "F89", {"style" : HoleStyle.C_SINK, "endStyle" : HoleEndStyle.BLIND, "holeDiameter" : 4 * mm, "cSinkDiameter" : 7.62 * mm, "cSinkAngle" : 82 * degree, "holeDepth" : 50.8 * mm, "tappedDepth" : 12.7 * mm, "tapClearance" : 3, "startFromSketch" : true, "locations" : qUnion([Q0, Q1]), "scope" : qUnion([Q2])});
        }
        {
            var Q0;
            Q0=makeQuery(id+"F45.boolean.opBoolean","MERGE",FACE,{"derivedFrom":[makeQuery(id+"F40.opExtrude","CAP_FACE",FACE,{"disambiguationData":[OSD([sQuery(id+"F39.wireOp",EDGE,"E56.bottom"),sQuery(id+"F39.wireOp",EDGE,"E56.top"),sQuery(id+"F39.wireOp",EDGE,"E56.left"),sQuery(id+"F39.wireOp",EDGE,"E56.right")])],"isStart":false}),makeQuery(id+"F45.opExtrude","SWEPT_FACE",FACE,{"disambiguationData":[OSD([sQuery(id+"F43.wireOp",EDGE,"E59.bottom")])]})]});
            var sketch = newSketch(context, id + "F90", { "sketchPlane" : qUnion([Q0])});
            skPoint(sketch, "E119", {"position": v(104.78, 57.15) * mm});
            skPoint(sketch, "E119.positionSnap0", {"position": v(104.78, 49.21) * mm});
            skSolve(sketch);
        }
        {
            var Q0;
            Q0=makeQuery(id+"F45.boolean.opBoolean","MERGE",FACE,{"derivedFrom":[makeQuery(id+"F40.opExtrude","CAP_FACE",FACE,{"disambiguationData":[OSD([sQuery(id+"F38.wireOp",EDGE,"E55.bottom"),sQuery(id+"F38.wireOp",EDGE,"E55.top"),sQuery(id+"F38.wireOp",EDGE,"E55.left"),sQuery(id+"F38.wireOp",EDGE,"E55.right")])],"isStart":false}),makeQuery(id+"F45.opExtrude","SWEPT_FACE",FACE,{"disambiguationData":[OSD([sQuery(id+"F44.wireOp",EDGE,"E60.bottom")])]})]});
            var sketch = newSketch(context, id + "F91", { "sketchPlane" : qUnion([Q0])});
            skPoint(sketch, "E120", {"position": v(-104.78, 57.15) * mm});
            skPoint(sketch, "E120.positionSnap0", {"position": v(-104.78, 49.21) * mm});
            skSolve(sketch);
        }
        {
            var Q0;
            Q0=sQuery(id+"F91.wireOp",VERTEX,"E120");
            var Q1;
            Q1=sQuery(id+"F90.wireOp",VERTEX,"E119");
            var Q2;
            Q2=makeQuery(id+"F40.opExtrude","SWEPT_BODY",BODY,{"disambiguationData":[OSD([sQuery(id+"F38.wireOp",EDGE,"E55.bottom"),sQuery(id+"F38.wireOp",EDGE,"E55.top"),sQuery(id+"F38.wireOp",EDGE,"E55.left"),sQuery(id+"F38.wireOp",EDGE,"E55.right")])]});
            hole(context, id + "F92", {"style" : HoleStyle.C_SINK, "endStyle" : HoleEndStyle.BLIND, "holeDiameter" : 4 * mm, "cSinkDiameter" : 7.62 * mm, "cSinkAngle" : 82 * degree, "holeDepth" : 50.8 * mm, "tappedDepth" : 12.7 * mm, "tapClearance" : 3, "startFromSketch" : true, "locations" : qUnion([Q0, Q1]), "scope" : qUnion([Q2])});
        }
        {
            var Q0;
            Q0=qCreatedBy(makeId("Right.planeOp"),FACE);
            cPlane(context, id + "F93", {"entities" : qUnion([Q0]), "cplaneType" : CPlaneType.OFFSET, "offset" : 79.38 * mm, "width" : 152.4 * mm, "height" : 152.4 * mm});
        }
        {
            var Q0;
            Q0=qCreatedBy(id+"F76.planeOp",FACE);
            var sketch = newSketch(context, id + "F94", { "sketchPlane" : qUnion([Q0])});
            skPoint(sketch, "E121.middle", {"position": v(0, 0) * mm});
            skPoint(sketch, "E122", {"position": v(-79.38, 165.4) * mm});
            skPoint(sketch, "E123", {"position": v(79.38, 165.4) * mm});
            skPoint(sketch, "E124", {"position": v(-79.38, -165.4) * mm});
            skPoint(sketch, "E125", {"position": v(79.38, -165.4) * mm});
            skPoint(sketch, "E126", {"position": v(0, 177.8) * mm});
            skPoint(sketch, "E127", {"position": v(0, -177.8) * mm});
            skArc(sketch, "E128", {"start": v(79.37, 165.4) * mm, "mid": v(0, 177.8) * mm, "end": v(-79.37, 165.4) * mm});
            skArc(sketch, "E129", {"start": v(-79.38, -165.4) * mm, "mid": v(0, -177.8) * mm, "end": v(79.37, -165.4) * mm});
            skPoint(sketch, "E121.bottom.end.orphan", {"position": v(-79.38, 196.39) * mm});
            skPoint(sketch, "E130.orphan", {"position": v(79.38, 196.39) * mm});
            skPoint(sketch, "E121.top.end.orphan", {"position": v(-79.38, -196.39) * mm});
            skPoint(sketch, "E121.left.end.orphan", {"position": v(79.38, -196.39) * mm});
            skSolve(sketch);
        }
        {
            var Q0;
            Q0=qCreatedBy(id+"F93.planeOp",FACE);
            var sketch = newSketch(context, id + "F95", { "sketchPlane" : qUnion([Q0])});
            skPoint(sketch, "E131", {"position": v(-115.89, 165.9) * mm});
            skCircle(sketch, "E132", {"center": v(-115.89, 165.9) * mm, "radius": 6.75 * mm});
            skSolve(sketch);
        }
        {
            var Q0;
            Q0 = qSketchRegion(id + "F95", true);
            var Q1;
            Q1=sQuery(id+"F94.wireOp",EDGE,"E128");
            sweep(context, id + "F96", {"operationType" : NewBodyOperationType.ADD, "profiles" : qUnion([Q0]), "path" : qUnion([Q1]), "keepProfileOrientation" : true});
        }
        {
            var Q0;
            Q0=qCreatedBy(id+"F93.planeOp",FACE);
            var sketch = newSketch(context, id + "F97", { "sketchPlane" : qUnion([Q0])});
            skPoint(sketch, "E133", {"position": v(-115.89, -165.9) * mm});
            skCircle(sketch, "E134", {"center": v(-115.89, -165.9) * mm, "radius": 6.75 * mm});
            skSolve(sketch);
        }
        {
            var Q0;
            Q0 = qSketchRegion(id + "F97", true);
            var Q1;
            Q1=sQuery(id+"F94.wireOp",EDGE,"E129");
            sweep(context, id + "F98", {"operationType" : NewBodyOperationType.ADD, "profiles" : qUnion([Q0]), "path" : qUnion([Q1]), "keepProfileOrientation" : true});
        }
        {
            var Q0;
            Q0=makeQuery(id+"F96.opSweep","CAP_EDGE",EDGE,{"disambiguationData":[OSD([sQuery(id+"F94.wireOp",VERTEX,"E128.start"),sQuery(id+"F95.wireOp",EDGE,"E132")])],"isStart":true});
            var Q1;
            Q1=makeQuery(id+"F96.opSweep","CAP_EDGE",EDGE,{"disambiguationData":[OSD([sQuery(id+"F94.wireOp",VERTEX,"E128.end"),sQuery(id+"F95.wireOp",EDGE,"E132")])],"isStart":false});
            var Q2;
            Q2=makeQuery(id+"F98.opSweep","CAP_EDGE",EDGE,{"disambiguationData":[OSD([sQuery(id+"F94.wireOp",VERTEX,"E129.end"),sQuery(id+"F97.wireOp",EDGE,"E134")])],"isStart":true});
            var Q3;
            Q3=makeQuery(id+"F98.opSweep","CAP_EDGE",EDGE,{"disambiguationData":[OSD([sQuery(id+"F94.wireOp",VERTEX,"E129.start"),sQuery(id+"F97.wireOp",EDGE,"E134")])],"isStart":false});
            fillet(context, id + "F99", {"entities" : qUnion([Q0, Q1, Q2, Q3]), "radius" : 3.17 * mm, "tangentPropagation" : true, "allowEdgeOverflow" : false});
        }
        {
            var Q0;
            Q0=qCreatedBy(makeId("Right.planeOp"),FACE);
            var sketch = newSketch(context, id + "F100", { "sketchPlane" : qUnion([Q0])});
            skLineSegment(sketch, "E135.bottom", {"start": v(25.4, 19.05) * mm, "end": v(-25.4, 19.05) * mm});
            skLineSegment(sketch, "E135.top", {"start": v(25.4, -19.05) * mm, "end": v(-25.4, -19.05) * mm});
            skLineSegment(sketch, "E135.left", {"start": v(25.4, 19.05) * mm, "end": v(25.4, -19.05) * mm});
            skLineSegment(sketch, "E135.right", {"start": v(-25.4, 19.05) * mm, "end": v(-25.4, -19.05) * mm});
            skPoint(sketch, "E135.middle", {"position": v(0, 0) * mm});
            skSolve(sketch);
        }
        {
            var Q0;
            Q0 = qSketchRegion(id + "F100", true);
            extrude(context, id + "F101", {"entities" : qUnion([Q0]), "endBound" : BoundingType.SYMMETRIC, "depth" : 152.4 * mm});
        }
        {
            var Q0;
            {var subQ0=sQuery(id+"F70.wireOp",EDGE,"E94");Q0=makeQuery(id+"F78.boolean.opBoolean","MERGE",EDGE,{"derivedFrom":[makeQuery(id+"F72.opExtrude","CAP_EDGE",EDGE,{"disambiguationData":[OSD([subQ0])],"isStart":false}),makeQuery(id+"F78.opSweep","CAP_EDGE",EDGE,{"disambiguationData":[OSD([subQ0,sQuery(id+"F77.wireOp",VERTEX,"E107.end")])],"isStart":true})]});}
            var Q1;
            Q1=makeQuery(id+"F78.boolean.opBoolean","MERGE",EDGE,{"derivedFrom":[makeQuery(id+"F75.opExtrude","CAP_EDGE",EDGE,{"disambiguationData":[OSD([sQuery(id+"F73.wireOp",EDGE,"E98")])],"isStart":false}),makeQuery(id+"F78.opSweep","CAP_EDGE",EDGE,{"disambiguationData":[OSD([sQuery(id+"F70.wireOp",EDGE,"E94"),sQuery(id+"F77.wireOp",VERTEX,"E107.start")])],"isStart":false})]});
            var Q2;
            Q2=makeQuery(id+"F79.boolean.opBoolean","MERGE",EDGE,{"derivedFrom":[makeQuery(id+"F75.opExtrude","CAP_EDGE",EDGE,{"disambiguationData":[OSD([sQuery(id+"F74.wireOp",EDGE,"E100")])],"isStart":false}),makeQuery(id+"F79.opSweep","CAP_EDGE",EDGE,{"disambiguationData":[OSD([sQuery(id+"F71.wireOp",EDGE,"E96"),sQuery(id+"F77.wireOp",VERTEX,"E108.end")])],"isStart":false})]});
            var Q3;
            {var subQ0=sQuery(id+"F71.wireOp",EDGE,"E96");Q3=makeQuery(id+"F79.boolean.opBoolean","MERGE",EDGE,{"derivedFrom":[makeQuery(id+"F72.opExtrude","CAP_EDGE",EDGE,{"disambiguationData":[OSD([subQ0])],"isStart":false}),makeQuery(id+"F79.opSweep","CAP_EDGE",EDGE,{"disambiguationData":[OSD([subQ0,sQuery(id+"F77.wireOp",VERTEX,"E108.start")])],"isStart":true})]});}
            fillet(context, id + "F102", {"entities" : qUnion([Q0, Q1, Q2, Q3]), "radius" : 4.6 * mm, "tangentPropagation" : true, "allowEdgeOverflow" : false});
        }
    });
